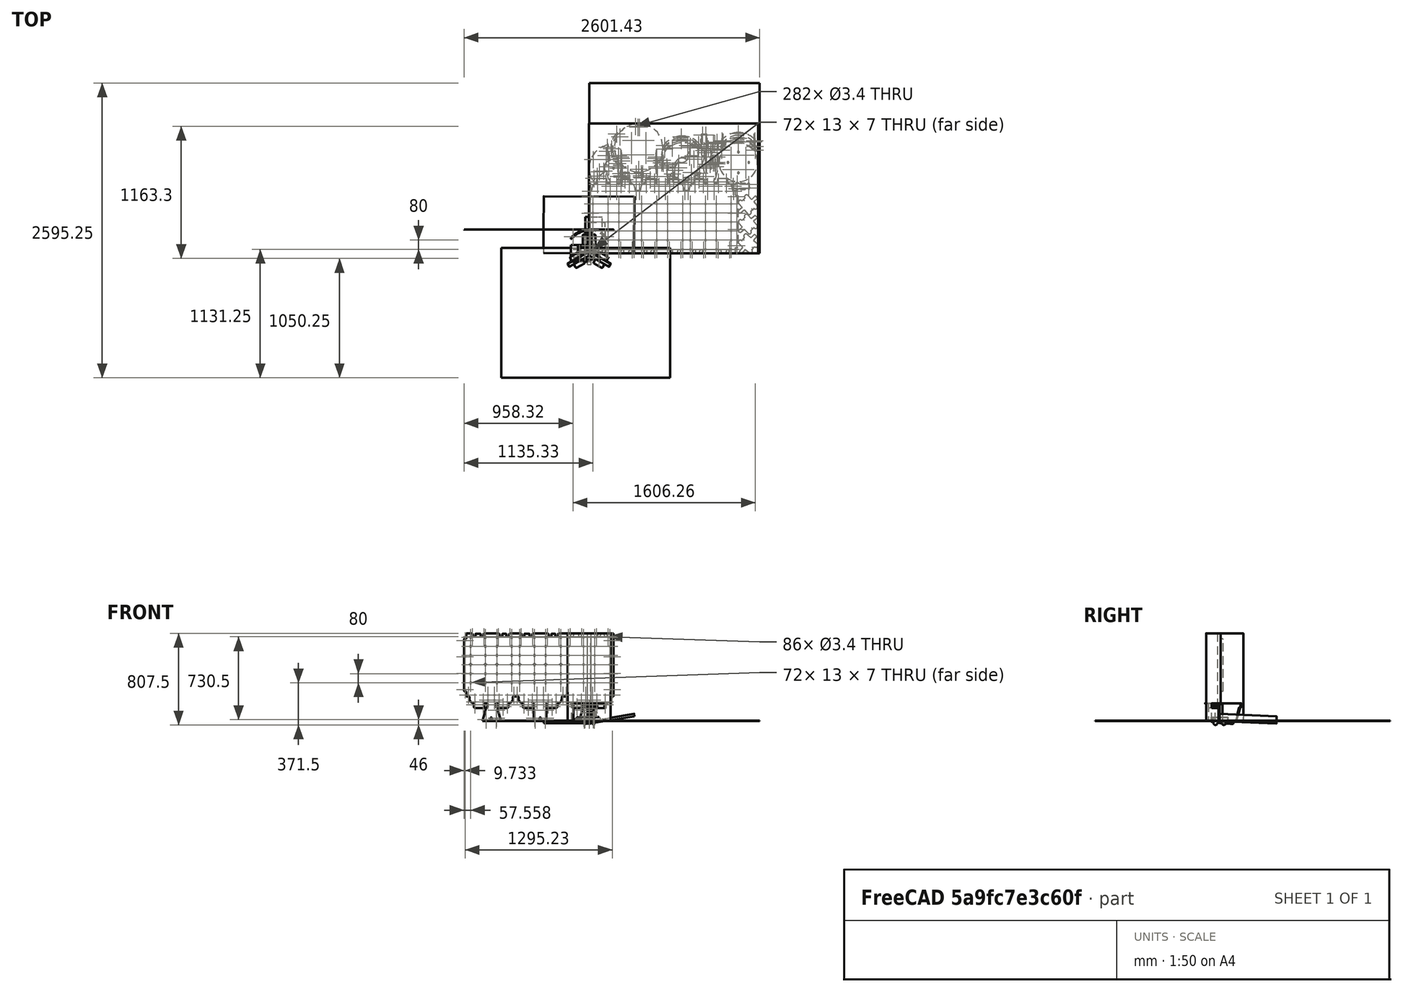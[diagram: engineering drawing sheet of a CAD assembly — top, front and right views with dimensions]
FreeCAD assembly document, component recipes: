
FREECAD ASSEMBLY — COMPONENT RECIPES ("composit_stand_small_3_vertDroppers")

This assembly document has 19 components, labeled P0..P18 below (a component is one placed body or linked part). 18 of them carry a construction recipe — the FreeCAD feature program that regenerates the part from scratch, quoted from this document or its linked companion documents; the rest are supplied as boundary geometry only. No exploded tour is included for this assembly.
NOTE — this tour is split across 2 documents so each fits a 32k-token context. This is document 1: the component sections continue in the remaining 1 document, each repeating the header above.
COMPONENT P0 — recipe-attached ("gutter001_material_0.50ansi", modeled in this document).
Construction recipe (the document's own serialized feature program — sketch geometry with constraints, then the solid features built on it; lengths are millimeters unless a unit is written):

FEATURE [Sketcher::SketchObject] Sketch  label="gutter_side_sketch"
  FullyConstrained = true
  MapMode = 5
  Support = -> [XY_Plane]
  expr: .AttachmentOffset.Base.x = 0
  expr: .Constraints.little_distance = <<gutter>>.low_edge_length + (<<main>>.inner_width - <<main>>.thickness * 2) / 2 - 3mm
  expr: Constraints[12] = <<gutter>>.length
  expr: Constraints[27] = <<gutter>>.bend_angle + 90°
  sketch-geometry (15):
    g0: LineSegment StartX=0 StartY=150 StartZ=0 EndX=13.5 EndY=150 EndZ=0
    g1: LineSegment StartX=27 StartY=0 StartZ=0 EndX=0 EndY=0 EndZ=0
    g2: LineSegment StartX=15 StartY=148.5 StartZ=0 EndX=15 EndY=120 EndZ=0
    g3: LineSegment StartX=15 StartY=120 StartZ=0 EndX=31.2589 EndY=120 EndZ=0
    g4: GeomPoint X=27 Y=150 Z=0
    g5: ArcOfCircle CenterX=31.2589 CenterY=116.5 CenterZ=0 NormalX=0 NormalY=0 NormalZ=1 AngleXU=0 Radius=3.5 StartAngle=6.21662 EndAngle=7.85398
    g6: GeomPoint X=27 Y=0 Z=0
    g7: ArcOfCircle CenterX=13.5 CenterY=148.5 CenterZ=0 NormalX=0 NormalY=0 NormalZ=1 AngleXU=0 Radius=1.5 StartAngle=-3.6e-15 EndAngle=1.5708
    g8: GeomPoint X=15 Y=150 Z=0
    g9: LineSegment StartX=34.7511 StartY=116.267 StartZ=0 EndX=27.4178 EndY=6.26718 EndZ=0
    g10: LineSegment StartX=27.4178 StartY=6.26718 StartZ=0 EndX=27 EndY=0 EndZ=0
    g11: ArcOfCircle CenterX=23.9256 CenterY=6.5 CenterZ=0 NormalX=0 NormalY=0 NormalZ=1 AngleXU=0 Radius=3.5 StartAngle=4.71239 EndAngle=6.21662
    g12: LineSegment StartX=0 StartY=0 StartZ=0 EndX=0 EndY=3 EndZ=0
    g13: LineSegment StartX=0 StartY=3 StartZ=0 EndX=0 EndY=150 EndZ=0
    g14: LineSegment StartX=0 StartY=3 StartZ=0 EndX=23.9256 EndY=3 EndZ=0
  constraints (36):
    c: Coincident(g-1,g12)
    c: PointOnObject(g13,g-2)
    c: Coincident(g13,g0)
    c: Horizontal(g0)
    c: PointOnObject(g6,g-1)
    c: Coincident(g1,g12)
    c: Distance(g1,g6) = 27  'little_distance'
    c: Vertical(g2)
    c: Coincident(g3,g2)
    c: Horizontal(g3)
    c: DistanceY(g2,g8) = 30
    c: PointOnObject(g4,g0)
    c: Distance(g6,g4) = 150
    c: Distance(g0,g8) = 15
    c: Tangent(g3,g5) = 1.5708
    c: Diameter(g5) = 7
    c: PointOnObject(g8,g0)
    c: PointOnObject(g8,g2)
    c: Tangent(g0,g7) = 1.5708
    c: Tangent(g2,g7) = 1.5708
    c: Diameter(g7) = 3
    c: Tangent(g9,g5) = 1.5708
    c: Vertical(g4,g6)
    c: Coincident(g1,g6)
    c: Coincident(g10,g1)
    c: Coincident(g9,g10)
    c: Parallel(g9,g10)
    c: Angle(g10,g-1) = 1.63736
    c: Coincident(g12,g13)
    c: Vertical(g12)
    c: Coincident(g14,g12)
    c: Horizontal(g14)
    c: Tangent(g11,g9) = 1.5708
    c: Tangent(g14,g11) = -1.5708
    c: Equal(g11,g5)
    c: DistanceY(g12,g12) = 3
FEATURE [PartDesign::Pad] Pad  label="gutter_side_pad"
  Direction = (0,0,1)
  Length = 0.3
  Length2 = 10
  Profile = -> Sketch
  ReferenceAxis = -> Sketch [N_Axis]
  Type = 0
FEATURE [Sketcher::SketchObject] Sketch010
  FullyConstrained = true
  MapMode = 5
  Support = -> [XY_Plane]
  expr: Constraints[2] = -(<<main>>.inner_width / 2 - <<main>>.thickness - <<main>>.bend_r)
  expr: Constraints[3] = <<gutter>>.length
  sketch-geometry (1):
    g0: LineSegment StartX=-9.99 StartY=0 StartZ=0 EndX=-9.99 EndY=150 EndZ=0
  constraints (4):
    c: PointOnObject(g0,g-1)
    c: Vertical(g0)
    c: DistanceX(g0) = -9.99
    c: DistanceY(g0) = 150
FEATURE [PartDesign::Mirrored] Mirrored005
  BaseFeature = -> Pad
  MirrorPlane = -> YZ_Plane
  Originals = -> [Pad]
  Refine = true
FEATURE [PartDesign::CoordinateSystem] Local_CS001
  AttacherType = Attacher::AttachEngine3D
  AttachmentOffset = pos=(-30,0,0) rot=(0,0,1;0.066568rad)
  MapMode = 5
  Placement = pos=(-30,0,0) rot=(0,0,1;0.066568rad)
  Support = -> [XY_Plane]
  expr: .AttachmentOffset.Base.x = -(<<gutter>>.low_edge_length + (<<main>>.inner_width - <<main>>.thickness * 2) / 2)
  expr: .AttachmentOffset.Rotation.Angle = <<gutter>>.bend_angle
  expr: .AttachmentOffset.Rotation.Yaw = <<gutter>>.bend_angle
FEATURE [PartDesign::CoordinateSystem] Local_CS002
  AttacherType = Attacher::AttachEngine3D
  AttachmentOffset = pos=(30,0,0) rot=(0,0,1;-0.066568rad)
  MapMode = 5
  Placement = pos=(30,0,0) rot=(0,0,1;6.21662rad)
  Support = -> [XY_Plane]
  expr: .AttachmentOffset.Base.x = <<gutter>>.low_edge_length + (<<main>>.inner_width - <<main>>.thickness * 2) / 2
  expr: .AttachmentOffset.Rotation.Angle = -<<gutter>>.bend_angle
FEATURE [PartDesign::CoordinateSystem] Local_CS003
  AttacherType = Attacher::AttachEngine3D
  AttachmentOffset = pos=(0,60,0) rot=(0,0,1;1.5708rad)
  MapMode = 5
  Placement = pos=(33.9911,59.8671,0) rot=(0,0,1;1.50423rad)
  Support = -> [Local_CS002]
  expr: .AttachmentOffset.Base.y = <<gutter>>.plane_middle
FEATURE [PartDesign::CoordinateSystem] Local_CS004
  AttacherType = Attacher::AttachEngine3D
  AttachmentOffset = pos=(2,60,0) rot=(0,0,1;-1.5708rad)
  MapMode = 5
  Placement = pos=(-31.9956,60.0001,0) rot=(0,0,1;4.77896rad)
  Support = -> [Local_CS001]
  expr: .AttachmentOffset.Base.y = <<gutter>>.plane_middle
FEATURE [PartDesign::Plane] DatumPlane003
  Length = 91.4351
  MapMode = 4
  Placement = pos=(33.9911,59.8671,0) rot=(0.023538,0.706911,0.706911;3.09453rad)
  ResizeMode = 0
  Support = -> [Local_CS003]
  Width = 62.5599
FEATURE [PartDesign::Plane] DatumPlane004
  Length = 91.4351
  MapMode = 4
  Placement = pos=(-31.9956,60.0001,0) rot=(0.998893,0.03326,0.03326;1.5719rad)
  ResizeMode = 0
  Support = -> [Local_CS004]
  Width = 62.5599
FEATURE [PartDesign::Plane] DatumPlane005
  AttachmentOffset = pos=(0,-1,0) rot=(0,0,1;0rad)
  Length = 202.865
  MapMode = 5
  Placement = pos=(34.9889,59.8006,0) rot=(0,0,1;1.50423rad)
  ResizeMode = 0
  Support = -> [Local_CS003]
  Width = 102.646
FEATURE [PartDesign::Plane] DatumPlane006
  Length = 202.865
  MapMode = 5
  Placement = pos=(-31.9956,60.0001,0) rot=(0,0,-1;1.50423rad)
  ResizeMode = 0
  Support = -> [Local_CS004]
  Width = 102.646
FEATURE [Sketcher::SketchObject] Sketch037
  AttachmentOffset = pos=(30,2,0) rot=(0,0,1;0rad)
  FullyConstrained = true
  MapMode = 5
  Placement = pos=(33.9911,89.9337,0) rot=(0,0,1;1.50423rad)
  Support = -> [Local_CS003]
  expr: .AttachmentOffset.Base.x = <<dropper>>.distance_between_droppers1 / 2
  expr: Constraints[10] = <<dropper>>.d
  sketch-geometry (8):
    g0: LineSegment StartX=0 StartY=11.625 StartZ=0 EndX=1 EndY=11.625 EndZ=0
    g1: ArcOfCircle CenterX=1 CenterY=0 CenterZ=0 NormalX=0 NormalY=0 NormalZ=1 AngleXU=0 Radius=11.625 StartAngle=0.450911 EndAngle=1.5708
    g2: ArcOfCircle CenterX=17.127 CenterY=0 CenterZ=0 NormalX=0 NormalY=0 NormalZ=1 AngleXU=0 Radius=3 StartAngle=0.25268 EndAngle=1.29556
    g3: LineSegment StartX=12.0914 StartY=4.53943 StartZ=0 EndX=17.9423 EndY=2.88708 EndZ=0
    g4: LineSegment StartX=0 StartY=11.625 StartZ=0 EndX=0 EndY=0 EndZ=0
    g5: LineSegment StartX=0 StartY=0 StartZ=0 EndX=21 EndY=0 EndZ=0
    g6: ArcOfCircle CenterX=21 CenterY=1 CenterZ=0 NormalX=0 NormalY=0 NormalZ=1 AngleXU=0 Radius=1 StartAngle=3.39427 EndAngle=4.71239
    g7: ArcOfCircle CenterX=12.3631 CenterY=5.5018 CenterZ=0 NormalX=0 NormalY=0 NormalZ=1 AngleXU=0 Radius=1 StartAngle=3.5925 EndAngle=4.43715
  constraints (22):
    c: PointOnObject(g0,g-2)
    c: Horizontal(g0)
    c: PointOnObject(g2,g-1)
    c: Tangent(g3,g2) = 1.5708
    c: Tangent(g1,g0) = 1.5708
    c: Coincident(g4,g0)
    c: Coincident(g4,g-1)
    c: Coincident(g5,g4)
    c: Diameter(g2) = 6
    c: Angle(g3,g-1) = 0.275238
    c: Diameter(g1) = 23.25
    c: PointOnObject(g1,g-1)
    c: Distance(g0) = 1
    c: Horizontal(g5)
    c: Tangent(g6,g5) = -1.5708
    c: Tangent(g6,g2) = 1.5708
    c: Diameter(g6) = 2
    c: Distance(g5) = 21
    c: Tangent(g3,g7) = -1.5708
    c: Tangent(g1,g7) = 1.5708
    c: Diameter(g7) = 2
    c: DistanceY(g2) = 2.88708  'arc_height'
FEATURE [PartDesign::Pocket] Pocket008
  BaseFeature = -> Mirrored005
  Direction = (0,0,-1)
  Length = 5
  Length2 = 5
  Midplane = true
  Profile = -> Sketch037
  ReferenceAxis = -> Sketch037 [N_Axis]
  Type = 1
FEATURE [PartDesign::Mirrored] Mirrored006
  MirrorPlane = -> Sketch037 [V_Axis]
FEATURE [PartDesign::Mirrored] Mirrored007
  MirrorPlane = -> DatumPlane003
FEATURE [PartDesign::MultiTransform] MultiTransform002
  BaseFeature = -> Pocket008
  Originals = -> [Pocket008]
  Transformations = -> [Mirrored006,Mirrored007]
FEATURE [PartDesign::SubShapeBinder] Binder
  AttacherType = Attacher::AttachEngine3D
  AttachmentOffset = pos=(35,0,0) rot=(0,0,1;0rad)
  BindCopyOnChange = 0
  BindMode = 0
  ClaimChildren = true
  Context = -> Body [Binder.]
  Fuse = false
  MakeFace = true
  MapMode = 5
  OffsetFill = false
  OffsetIntersection = false
  OffsetJoinType = 0
  OffsetOpenResult = false
  PartialLoad = false
  Placement = pos=(-28.1674,25.0777,0) rot=(0,0,-1;1.50423rad)
  Relative = false
  _Version = 2
  expr: .AttachmentOffset.Base.x = <<dropper>>.distance_between_droppers2 / 2
FEATURE [PartDesign::Pocket] Pocket009
  BaseFeature = -> MultiTransform002
  Direction = (0,0,-1)
  Length = 5
  Length2 = 5
  Midplane = true
  Profile = -> Binder
  Type = 1
FEATURE [PartDesign::Plane] DatumPlane007
  Length = 91.4351
  MapMode = 4
  Placement = pos=(-28.1674,25.0777,0) rot=(0.998893,0.03326,0.03326;1.5719rad)
  ResizeMode = 0
  Support = -> [Binder]
  Width = 62.5599
FEATURE [PartDesign::Mirrored] Mirrored008
  MirrorPlane = -> DatumPlane007
FEATURE [PartDesign::Mirrored] Mirrored009
  MirrorPlane = -> DatumPlane004
FEATURE [PartDesign::MultiTransform] MultiTransform003
  BaseFeature = -> Pocket009
  Originals = -> [Pocket009]
  Transformations = -> [Mirrored008,Mirrored009]
FEATURE [Sketcher::SketchObject] Sketch038
  FullyConstrained = true
  MapMode = 5
  Support = -> [XY_Plane]
  expr: Constraints[2] = <<main>>.inner_width / 2 - <<main>>.thickness - <<main>>.bend_r
  expr: Constraints[3] = <<gutter>>.length
  sketch-geometry (1):
    g0: LineSegment StartX=9.99 StartY=0 StartZ=0 EndX=9.99 EndY=150 EndZ=0
  constraints (4):
    c: PointOnObject(g0,g-1)
    c: Vertical(g0)
    c: DistanceX(g0) = 9.99
    c: DistanceY(g0) = 150
FEATURE [Sketcher::SketchObject] Sketch039
  AttachmentOffset = pos=(51,14,0) rot=(0,0,1;0rad)
  FullyConstrained = true
  MapMode = 5
  Placement = pos=(24.4124,111.619,0) rot=(0,0,1;1.50423rad)
  Support = -> [DatumPlane005]
  expr: .AttachmentOffset.Base.x = <<main>>.gutter_fix_holes_distance
  expr: Constraints[1] = <<main>>.rivet_d
  sketch-geometry (1):
    g0: Circle CenterX=0 CenterY=0 CenterZ=0 NormalX=0 NormalY=0 NormalZ=1 AngleXU=0 Radius=1.7
  constraints (2):
    c: Coincident(g0,g-1)
    c: Diameter(g0) = 3.4
FEATURE [PartDesign::Pocket] Pocket010
  BaseFeature = -> MultiTransform003
  Direction = (0,0,-1)
  Length = 5
  Length2 = 5
  Midplane = true
  Profile = -> Sketch039
  ReferenceAxis = -> Sketch039 [N_Axis]
  Type = 1
FEATURE [PartDesign::Mirrored] Mirrored010
  MirrorPlane = -> DatumPlane003
FEATURE [PartDesign::Mirrored] Mirrored011
  MirrorPlane = -> YZ_Plane
FEATURE [PartDesign::MultiTransform] MultiTransform004
  BaseFeature = -> Pocket010
  Originals = -> [Pocket010]
  Transformations = -> [Mirrored010,Mirrored011]
FEATURE [PartDesign::FeaturePython] Fold  # WARN: FeaturePython — macro-defined, semantics opaque (R4)
  BaseFeature = -> MultiTransform004
  BendLine = -> Sketch038
  Position = 0
  angle = 90
  baseObject = -> MultiTransform004 [Face4]
  invert = false
  invertbend = true
  kfactor = 0.01
  radius = 0.01
  unfold = false
  expr: radius = <<main>>.bend_r
FEATURE [PartDesign::FeaturePython] Fold002  # WARN: FeaturePython — macro-defined, semantics opaque (R4)
  BaseFeature = -> Fold
  BendLine = -> Sketch010
  Position = 0
  angle = 90
  baseObject = -> Fold [Face2]
  invert = false
  invertbend = false
  kfactor = 0.01
  radius = 0.01
  unfold = false
  expr: radius = <<main>>.bend_r
FEATURE [PartDesign::CoordinateSystem] Local_CS024
  AttacherType = Attacher::AttachEngine3D
  AttachmentOffset = pos=(0,60,-10.3215) rot=(-1,0,0;0.066568rad)
  MapMode = 5
  Placement = pos=(0,60,-10.3215) rot=(-1,0,0;0.066568rad)
  Support = -> [XY_Plane]
  expr: .AttachmentOffset.Base.y = <<gutter>>.plane_middle
  expr: .AttachmentOffset.Base.z = (-6.929mm - 13.714mm) / 2
  expr: .AttachmentOffset.Rotation.Roll = -<<gutter>>.bend_angle
FEATURE [Sketcher::SketchObject] Sketch115
  FullyConstrained = true
  MapMode = 5
  Support = -> [XY_Plane]
  expr: Constraints[1] = <<main>>.rivet_d
  sketch-geometry (1):
    g0: Circle CenterX=0 CenterY=145 CenterZ=0 NormalX=0 NormalY=0 NormalZ=1 AngleXU=0 Radius=1.7
  constraints (3):
    c: PointOnObject(g0,g-2)
    c: Diameter(g0) = 3.4
    c: DistanceY(g0) = 145
FEATURE [PartDesign::Pocket] Pocket070
  BaseFeature = -> Fold002
  Direction = (0,0,-1)
  Length = 5
  Length2 = 5
  Midplane = true
  Profile = -> Sketch115
  ReferenceAxis = -> Sketch115 [N_Axis]
  Type = 1
FEATURE [PartDesign::Body] Body  label="gutter001_material_0.50ansi"
  Group = -> [Sketch,Pad,Mirrored005,Local_CS001,Local_CS002,Local_CS003,Local_CS004,DatumPlane003,DatumPlane004,DatumPlane005,DatumPlane006,Sketch037,Pocket008,MultiTransform002,Mirrored006,Mirrored007,Binder,Pocket009,MultiTransform003,Mirrored008,DatumPlane007,Mirrored009,Sketch010,Sketch038,Sketch039,Pocket010,MultiTransform004,Mirrored010,Mirrored011,Fold,Fold002,Local_CS024,Sketch115,Pocket070]
  Origin = -> Origin
  Tip = -> Pocket070
COMPONENT P1 — recipe-attached ("Body001_material_0.30ansi", modeled in this document).
Construction recipe (the document's own serialized feature program — sketch geometry with constraints, then the solid features built on it; lengths are millimeters unless a unit is written):

FEATURE [Sketcher::SketchObject] Sketch003  label="main_sketch"
  FullyConstrained = true
  MapMode = 5
  Support = -> [XY_Plane001]
  expr: Constraints[30] = <<main>>.end_face_width
  expr: Constraints[31] = <<main>>.work_plane_width
  expr: Constraints[44] = <<main>>.al_thickness
  sketch-geometry (17):
    g0: LineSegment StartX=-16 StartY=9.2376 StartZ=0 EndX=-16 EndY=209.238 EndZ=0
    g1: LineSegment StartX=-16 StartY=209.238 StartZ=0 EndX=16 EndY=209.238 EndZ=0
    g2: LineSegment StartX=16 StartY=209.238 StartZ=0 EndX=16 EndY=9.2376 EndZ=0
    g3: LineSegment StartX=16 StartY=9.2376 StartZ=0 EndX=189.205 EndY=-90.7624 EndZ=0
    g4: LineSegment StartX=189.205 StartY=-90.7624 StartZ=0 EndX=173.205 EndY=-118.475 EndZ=0
    g5: LineSegment StartX=173.205 StartY=-118.475 StartZ=0 EndX=0 EndY=-18.4752 EndZ=0
    g6: LineSegment StartX=0 StartY=-18.4752 StartZ=0 EndX=-173.205 EndY=-118.475 EndZ=0
    g7: LineSegment StartX=-173.205 StartY=-118.475 StartZ=0 EndX=-189.205 EndY=-90.7624 EndZ=0
    g8: LineSegment StartX=-189.205 StartY=-90.7624 StartZ=0 EndX=-16 EndY=9.2376 EndZ=0
    g9: LineSegment StartX=-16 StartY=9.2376 StartZ=0 EndX=0 EndY=0 EndZ=0
    g10: LineSegment StartX=0 StartY=0 StartZ=0 EndX=16 EndY=9.2376 EndZ=0
    g11: LineSegment StartX=0 StartY=0 StartZ=0 EndX=0 EndY=-18.4752 EndZ=0
    g12: LineSegment StartX=189.205 StartY=-90.7624 StartZ=0 EndX=13 EndY=10.9697 EndZ=0
    g13: LineSegment StartX=16 StartY=209.238 StartZ=0 EndX=16 EndY=9.42236 EndZ=0
    g14: LineSegment StartX=16 StartY=9.42236 StartZ=0 EndX=15.7 EndY=9.42236 EndZ=0
    g15: LineSegment StartX=13 StartY=10.9697 StartZ=0 EndX=13 EndY=30.9697 EndZ=0
    g16: LineSegment StartX=13 StartY=10.9697 StartZ=0 EndX=6.66667 EndY=0 EndZ=0
  constraints (56):
    c: Vertical(g0)
    c: Coincident(g0,g1)
    c: Horizontal(g1)
    c: Coincident(g1,g2)
    c: Vertical(g2)
    c: Coincident(g2,g3)
    c: Coincident(g3,g4)
    c: Coincident(g4,g5)
    c: PointOnObject(g5,g-2)
    c: Coincident(g5,g6)
    c: Coincident(g6,g7)
    c: Coincident(g8,g7)
    c: Equal(g2,g6)
    c: Equal(g6,g5)
    c: Equal(g5,g3)
    c: Equal(g4,g7)
    c: Equal(g7,g1)
    c: Perpendicular(g4,g5)
    c: Perpendicular(g4,g3)
    c: Perpendicular(g7,g6)
    c: Perpendicular(g8,g7)
    c: Angle(g6,g5) = 2.0944
    c: Angle(g3,g2) = 2.0944
    c: Coincident(g9,g0)
    c: Coincident(g9,g-1)
    c: Coincident(g10,g9)
    c: Coincident(g10,g2)
    c: Coincident(g11,g9)
    c: Coincident(g11,g5)
    c: Equal(g10,g11)
    c: DistanceX(g1,g1) = 32
    c: DistanceY(g2,g2) = 200
    c: DistanceY(g9,g2) = 9.2376  'petal_offset'
    c: DistanceY(g0) = 9.2376  'petal_conn_y'
    c: Coincident(g8,g0)
    c: DistanceX(g2) = 16  'petal_conn_x'
    c: Distance(g9,g1) = 209.848  'max_r'
    c: Distance(g10) = 18.4752  'planes_intersec_r'
    c: DistanceY(g9,g1) = 209.238  'total_petal_length'
    c: Coincident(g12,g4)
    c: Coincident(g13,g1)
    c: PointOnObject(g13,g2)
    c: Coincident(g14,g13)
    c: Horizontal(g14)
    c: DistanceX(g14,g14) = 0.3
    c: Distance(g14,g12) = 0.01
    c: PointOnObject(g2,g12)
    c: Distance(g12,g13) = 3
    c: Coincident(g15,g12)
    c: Vertical(g15)
    c: DistanceY(g15,g15) = 20
    c: DistanceY(g15) = 30.9697  'overlap_end_y'
    c: Coincident(g16,g12)
    c: Perpendicular(g16,g12)
    c: Distance(g9,g16) = 5.7735  'overlap_bend_offset'
    c: PointOnObject(g16,g-1)
FEATURE [PartDesign::FeaturePython] BaseBend001  # WARN: FeaturePython — macro-defined, semantics opaque (R4)
  BendSide = 0
  BendSketch = -> Sketch003
  MidPlane = false
  Reverse = false
  length = 774
  radius = 0.01
  thickness = 0.3
  expr: length = <<main>>.total_length
  expr: radius = <<main>>.bend_r
FEATURE [PartDesign::CoordinateSystem] Local_CS
  AttacherType = Attacher::AttachEngine3D
  AttachmentOffset = pos=(0,9.2376,0) rot=(0,0,1;0rad)
  MapMode = 5
  Placement = pos=(0,9.2376,0) rot=(0,0,1;0rad)
  Support = -> [XY_Plane001]
  expr: .AttachmentOffset.Base.y = Sketch003.Constraints.petal_offset
FEATURE [PartDesign::CoordinateSystem] Local_CS011
  AttacherType = Attacher::AttachEngine3D
  AttachmentOffset = pos=(0,100,0) rot=(0,0,1;0rad)
  MapMode = 5
  Placement = pos=(0,109.238,0) rot=(0,0,1;0rad)
  Support = -> [Local_CS]
  expr: .AttachmentOffset.Base.y = <<main>>.work_plane_width / 2
FEATURE [PartDesign::Plane] DatumPlane011
  AttachmentOffset = pos=(0,0,0) rot=(0,0,1;0.523599rad)
  Length = 594.137
  MapMode = 5
  Placement = pos=(0,0,0) rot=(0,0,1;0.523599rad)
  ResizeMode = 0
  Support = -> [XY_Plane001]
  Width = 579.207
FEATURE [PartDesign::CoordinateSystem] Local_CS035
  AttacherType = Attacher::AttachEngine3D
  AttachmentOffset = pos=(0,0,774) rot=(0,0,1;0rad)
  MapMode = 5
  Placement = pos=(0,109.238,774) rot=(0,0,1;0rad)
  Support = -> [Local_CS011]
  expr: .AttachmentOffset.Base.z = <<main>>.total_length
FEATURE [PartDesign::CoordinateSystem] Local_CS036  label="droppers_center"
  AttacherType = Attacher::AttachEngine3D
  AttachmentOffset = pos=(0,0,-19) rot=(0,0,1;0rad)
  MapMode = 5
  Placement = pos=(0,109.238,755) rot=(0,0,1;0rad)
  Support = -> [Local_CS035]
FEATURE [PartDesign::CoordinateSystem] Local_CS037  label="gutter_fixture_center"
  AttacherType = Attacher::AttachEngine3D
  AttachmentOffset = pos=(0,0,-12) rot=(0,0,1;0rad)
  MapMode = 5
  Placement = pos=(0,109.238,743) rot=(0,0,1;0rad)
  Support = -> [Local_CS036]
FEATURE [PartDesign::CoordinateSystem] Local_CS038  label="modules_top_center"
  AttacherType = Attacher::AttachEngine3D
  AttachmentOffset = pos=(0,0,-5) rot=(0,0,1;0rad)
  MapMode = 5
  Placement = pos=(0,109.238,738) rot=(0,0,1;0rad)
  Support = -> [Local_CS037]
FEATURE [Sketcher::SketchObject] Sketch112
  FullyConstrained = true
  MapMode = 5
  Placement = pos=(0,0,0) rot=(0.57735,0.57735,0.57735;2.0944rad)
  Support = -> [YZ_Plane001]
  expr: Constraints[10] = <<module>>.module_hole_x
  expr: Constraints[11] = <<module>>.module_hole_y
  sketch-geometry (5):
    g0: LineSegment StartX=-6.5 StartY=-3.5 StartZ=0 EndX=-6.5 EndY=3.5 EndZ=0
    g1: LineSegment StartX=-6.5 StartY=3.5 StartZ=0 EndX=6.5 EndY=3.5 EndZ=0
    g2: LineSegment StartX=6.5 StartY=3.5 StartZ=0 EndX=6.5 EndY=-3.5 EndZ=0
    g3: LineSegment StartX=6.5 StartY=-3.5 StartZ=0 EndX=-6.5 EndY=-3.5 EndZ=0
    g4: GeomPoint X=0 Y=0 Z=0
  constraints (12):
    c: Coincident(g0,g1)
    c: Coincident(g1,g2)
    c: Coincident(g2,g3)
    c: Coincident(g3,g0)
    c: Horizontal(g1)
    c: Horizontal(g3)
    c: Vertical(g0)
    c: Vertical(g2)
    c: Symmetric(g1,g0,g4)
    c: Coincident(g4,g-1)
    c: DistanceX(g1,g1) = 13
    c: DistanceY(g2,g2) = 7
FEATURE [Sketcher::SketchObject] Sketch113
  FullyConstrained = true
  MapMode = 5
  Placement = pos=(0,0,0) rot=(0.57735,0.57735,0.57735;2.0944rad)
  Support = -> [YZ_Plane001]
  expr: Constraints[18] = <<dropper>>.d + 2mm
  expr: Constraints[19] = <<dropper>>.center_height_offset
  sketch-geometry (8):
    g0: ArcOfCircle CenterX=0 CenterY=0 CenterZ=0 NormalX=0 NormalY=0 NormalZ=1 AngleXU=0 Radius=12.625 StartAngle=3.14159 EndAngle=6.28319
    g1: LineSegment StartX=12.625 StartY=-3.1e-15 StartZ=0 EndX=12.625 EndY=12.5 EndZ=0
    g2: LineSegment StartX=-12.625 StartY=1.5e-15 StartZ=0 EndX=-12.625 EndY=12.5 EndZ=0
    g3: ArcOfCircle CenterX=15.125 CenterY=12.5 CenterZ=0 NormalX=0 NormalY=0 NormalZ=1 AngleXU=0 Radius=2.5 StartAngle=1.5708 EndAngle=3.14159
    g4: ArcOfCircle CenterX=-15.125 CenterY=12.5 CenterZ=0 NormalX=0 NormalY=0 NormalZ=1 AngleXU=0 Radius=2.5 StartAngle=0 EndAngle=1.5708
    g5: LineSegment StartX=-15.125 StartY=15 StartZ=0 EndX=-15.125 EndY=19 EndZ=0
    g6: LineSegment StartX=-15.125 StartY=19 StartZ=0 EndX=15.125 EndY=19 EndZ=0
    g7: LineSegment StartX=15.125 StartY=19 StartZ=0 EndX=15.125 EndY=15 EndZ=0
  constraints (24):
    c: Coincident(g0,g-1)
    c: PointOnObject(g0,g-1)
    c: PointOnObject(g0,g-1)
    c: Coincident(g1,g0)
    c: Vertical(g1)
    c: Coincident(g2,g0)
    c: Vertical(g2)
    c: Coincident(g5,g4)
    c: Vertical(g5)
    c: Coincident(g6,g5)
    c: Horizontal(g6)
    c: Coincident(g7,g6)
    c: Coincident(g7,g3)
    c: Vertical(g7)
    c: Perpendicular(g3,g7)
    c: Tangent(g3,g1) = 1.5708
    c: Tangent(g4,g2) = -1.5708
    c: Perpendicular(g4,g5)
    c: Diameter(g0) = 25.25
    c: Distance(g0,g6) = 19
    c: Equal(g4,g3)
    c: Diameter(g4) = 5
    c: DistanceY(g7,g7) = 4
    c: Equal(g5,g7)
FEATURE [Sketcher::SketchObject] Sketch128
  FullyConstrained = true
  MapMode = 5
  Placement = pos=(0,0,0) rot=(0.57735,0.57735,0.57735;2.0944rad)
  Support = -> [YZ_Plane001]
  expr: Constraints[5] = <<main>>.basin_height
  sketch-geometry (5):
    g0: LineSegment StartX=73 StartY=116.5 StartZ=0 EndX=166 EndY=116.5 EndZ=0
    g1: LineSegment StartX=166 StartY=116.5 StartZ=0 EndX=166 EndY=157 EndZ=0
    g2: LineSegment StartX=166 StartY=157 StartZ=0 EndX=73 EndY=157 EndZ=0
    g3: LineSegment StartX=73 StartY=157 StartZ=0 EndX=73 EndY=116.5 EndZ=0
    g4: GeomPoint X=119.5 Y=157 Z=0
  constraints (15):
    c: Coincident(g0,g1)
    c: Coincident(g1,g2)
    c: Coincident(g2,g3)
    c: Coincident(g3,g0)
    c: DistanceX(g0) = 73  'offset_x'
    c: DistanceY(g2) = 157
    c: Distance(g3) = 40.5  'height'
    c: Distance(g0) = 93  'length'
    c: Parallel(g1,g3)
    c: Parallel(g0,g2)
    c: Perpendicular(g0,g3)
    c: Angle(g-1,g0) = 0
    c: Symmetric(g2,g1,g4)
    c: DistanceX(g4) = 119.5  'top_center_x'
    c: DistanceY(g4) = 157  'top_center_y'
FEATURE [PartDesign::Pocket] Pocket081
  BaseFeature = -> BaseBend001
  Direction = (-1,2e-16,-3e-16)
  Length = 5
  Length2 = 5
  Midplane = true
  Profile = -> Sketch128
  ReferenceAxis = -> Sketch128 [N_Axis]
  Type = 1
FEATURE [PartDesign::PolarPattern] PolarPattern016
  Angle = 360
  Axis = -> Z_Axis001
  BaseFeature = -> Pocket081
  Occurrences = 3
  Originals = -> [Pocket081]
FEATURE [PartDesign::FeaturePython] Bend  # WARN: FeaturePython — macro-defined, semantics opaque (R4)
  AutoMiter = true
  BaseFeature = -> PolarPattern016
  BendType = 0
  LengthList = [40]
  LengthSpec = 2
  ReliefFactor = 0.7
  UseReliefFactor = false
  angle = 90
  baseObject = -> PolarPattern016 [Edge67,Edge25,Edge211,Edge168,Edge96,Edge140]
  bendAList = [90]
  extend1 = 0
  extend2 = 0
  gap1 = 0.1
  gap2 = 0.1
  invert = false
  kfactor = 0.5
  length = 40
  maxExtendDist = 5
  minGap = 0.1
  minReliefGap = 1
  miterangle1 = 0
  miterangle2 = 0
  offset = 0
  radius = 0.1
  reliefType = 0
  reliefd = 1
  reliefw = 0.8
  sketchflip = false
  sketchinvert = false
  unfold = false
  expr: angle = 90deg - <<main>>.cover_bend_mid
FEATURE [PartDesign::Pocket] Pocket007
  BaseFeature = -> Bend
  Direction = (-1,2e-16,-3e-16)
  Length = 13.01
  Length2 = 5
  Profile = -> Sketch012
  ReferenceAxis = -> Sketch012 [N_Axis]
  Reversed = true
  Type = 0
  expr: Length = <<main>>.end_face_width / 2 - <<main>>.thickness + <<main>>.bend_r
FEATURE [Sketcher::SketchObject] Sketch129
  AttachmentOffset = pos=(0,0,0) rot=(0,1,0;3.66519rad)
  FullyConstrained = true
  MapMode = 5
  Placement = pos=(0,0,0) rot=(-0.186157,0.694747,0.694747;3.50969rad)
  Support = -> [XZ_Plane001]
  expr: .Constraints.height = Sketch128.Constraints.height
  expr: .Constraints.length = Sketch128.Constraints.length
  expr: Constraints[20] = <<main>>.cover_plane_bend
  expr: Constraints[24] = Sketch128.Constraints.top_center_x
  expr: Constraints[25] = Sketch128.Constraints.top_center_y
  expr: Constraints[8] = <<main>>.basin_height
  sketch-geometry (10):
    g0: LineSegment StartX=0 StartY=0 StartZ=0 EndX=169.18 EndY=0 EndZ=0
    g1: LineSegment StartX=169.18 StartY=0 StartZ=0 EndX=169.18 EndY=157 EndZ=0
    g2: LineSegment StartX=0 StartY=157 StartZ=0 EndX=0 EndY=0 EndZ=0
    g3: LineSegment StartX=73 StartY=116.5 StartZ=0 EndX=166 EndY=116.5 EndZ=0
    g4: LineSegment StartX=166 StartY=116.5 StartZ=0 EndX=166 EndY=157 EndZ=0
    g5: LineSegment StartX=166 StartY=157 StartZ=0 EndX=73 EndY=157 EndZ=0
    g6: LineSegment StartX=73 StartY=157 StartZ=0 EndX=73 EndY=116.5 EndZ=0
    g7: LineSegment StartX=169.18 StartY=157 StartZ=0 EndX=166 EndY=157 EndZ=0
    g8: LineSegment StartX=73 StartY=157 StartZ=0 EndX=0 EndY=157 EndZ=0
    g9: GeomPoint X=119.5 Y=157 Z=0
  constraints (26):
    c: Coincident(g0,g1)
    c: Coincident(g1,g7)
    c: Coincident(g8,g2)
    c: Coincident(g2,g0)
    c: Horizontal(g0)
    c: Vertical(g1)
    c: Vertical(g2)
    c: Coincident(g0,g-1)
    c: DistanceY(g8) = 157
    c: Coincident(g3,g4)
    c: Coincident(g4,g5)
    c: Coincident(g5,g6)
    c: Coincident(g6,g3)
    c: Horizontal(g7)
    c: Coincident(g8,g5)
    c: Coincident(g7,g4)
    c: Perpendicular(g4,g3)
    c: Perpendicular(g5,g4)
    c: Perpendicular(g5,g6)
    c: Distance(g3,g1) = 3.18
    c: Angle(g-1,g5) = 0
    c: Distance(g6) = 40.5  'height'
    c: Distance(g3) = 93  'length'
    c: Symmetric(g6,g4,g9)
    c: DistanceX(g9) = 119.5
    c: DistanceY(g9) = 157
FEATURE [PartDesign::CoordinateSystem] Local_CS041
  AttacherType = Attacher::AttachEngine3D
  AttachmentOffset = pos=(119.5,157,16) rot=(0,-0.707107,-0.707107;3.14159rad)
  MapMode = 5
  Placement = pos=(16,119.5,157) rot=(0,0,-1;1.5708rad)
  Support = -> [YZ_Plane001]
  expr: .AttachmentOffset.Base.x = Sketch128.Constraints.top_center_x
  expr: .AttachmentOffset.Base.y = Sketch128.Constraints.top_center_y
  expr: .AttachmentOffset.Base.z = <<main>>.end_face_width / 2
FEATURE [PartDesign::CoordinateSystem] Local_CS039
  AttacherType = Attacher::AttachEngine3D
  AttachmentOffset = pos=(0,-3,-3) rot=(0,1,0.71;0rad)
  MapMode = 5
  Placement = pos=(13,119.5,154) rot=(0,0,-1;1.5708rad)
  Support = -> [Local_CS041]
  expr: .AttachmentOffset.Base.y = -<<main>>.thickness
  expr: .AttachmentOffset.Base.z = -<<main>>.thickness
FEATURE [Sketcher::SketchObject] Sketch130
  AttachmentOffset = pos=(0,40.5,0) rot=(0,0,1;0rad)
  FullyConstrained = true
  MapMode = 5
  Placement = pos=(56.5,119.5,157) rot=(0,0,-1;1.5708rad)
  Support = -> [Local_CS041]
  expr: .AttachmentOffset.Base.y = Bend.length + 0.5mm
  expr: Constraints[14] = Sketch128.Constraints.length
  sketch-geometry (6):
    g0: ArcOfCircle CenterX=36.5 CenterY=-10 CenterZ=0 NormalX=0 NormalY=0 NormalZ=1 AngleXU=0 Radius=10 StartAngle=6.28318 EndAngle=7.85398
    g1: ArcOfCircle CenterX=-36.5 CenterY=-10 CenterZ=0 NormalX=0 NormalY=0 NormalZ=1 AngleXU=0 Radius=10 StartAngle=1.5708 EndAngle=3.14159
    g2: LineSegment StartX=-46.5 StartY=-10 StartZ=0 EndX=-46.5 EndY=0 EndZ=0
    g3: LineSegment StartX=-36.5 StartY=0 StartZ=0 EndX=-46.5 EndY=0 EndZ=0
    g4: LineSegment StartX=46.5 StartY=-10 StartZ=0 EndX=46.5 EndY=0 EndZ=0
    g5: LineSegment StartX=36.5 StartY=0 StartZ=0 EndX=46.5 EndY=0 EndZ=0
  constraints (17):
    c: PointOnObject(g0,g-1)
    c: PointOnObject(g1,g-1)
    c: Coincident(g2,g1)
    c: PointOnObject(g2,g-1)
    c: Vertical(g2)
    c: Tangent(g2,g1)
    c: Coincident(g3,g2)
    c: Coincident(g4,g0)
    c: PointOnObject(g4,g-1)
    c: Vertical(g4)
    c: Tangent(g4,g0)
    c: Coincident(g5,g4)
    c: Tangent(g5,g0) = 1.5708
    c: Tangent(g3,g1) = -1.5708
    c: DistanceX(g2,g4) = 93
    c: Symmetric(g1,g0,g-2)
    c: Diameter(g0) = 20
FEATURE [PartDesign::Mirrored] Mirrored040
  MirrorPlane = -> YZ_Plane001
FEATURE [PartDesign::PolarPattern] PolarPattern017
  Angle = 360
  Axis = -> Z_Axis001
  Occurrences = 3
FEATURE [PartDesign::CoordinateSystem] Local_CS042
  AttacherType = Attacher::AttachEngine3D
  AttachmentOffset = pos=(0,0,0) rot=(0,0,1;2.0944rad)
  MapMode = 5
  Placement = pos=(0,0,0) rot=(0,0,1;2.0944rad)
  Support = -> [XY_Plane001]
FEATURE [PartDesign::CoordinateSystem] Local_CS012
  AttacherType = Attacher::AttachEngine3D
  AttachmentOffset = pos=(16,119.5,157) rot=(0,0,-1;1.5708rad)
  MapMode = 5
  Placement = pos=(-111.49,-45.8936,157) rot=(0,0,1;0.523599rad)
  Support = -> [Local_CS042]
  expr: AttachmentOffset = Local_CS041.Placement
FEATURE [PartDesign::Plane] DatumPlane012
  Length = 594.137
  MapMode = 5
  Placement = pos=(-111.49,-45.8936,157) rot=(0,0,1;0.523599rad)
  ResizeMode = 0
  Support = -> [Local_CS012]
  Width = 579.207
FEATURE [PartDesign::Pocket] Pocket091
  BaseFeature = -> Pocket007
  Direction = (-0.5,-0.866025,-1e-16)
  Length = 16
  Length2 = 5
  Profile = -> Sketch134
  ReferenceAxis = -> Sketch134 [N_Axis]
  Refine = true
  Reversed = true
  Type = 0
  expr: Length = <<main>>.end_face_width / 2
FEATURE [Sketcher::SketchObject] Sketch136
  FullyConstrained = true
  MapMode = 5
  Support = -> [XY_Plane001]
  sketch-geometry (6):
    g0: LineSegment StartX=0 StartY=-100 StartZ=0 EndX=-86.6025 EndY=50 EndZ=0
    g1: LineSegment StartX=-86.6025 StartY=50 StartZ=0 EndX=86.6025 EndY=50 EndZ=0
    g2: LineSegment StartX=86.6025 StartY=50 StartZ=0 EndX=0 EndY=-100 EndZ=0
    g3: LineSegment StartX=-86.6025 StartY=50 StartZ=0 EndX=0 EndY=7.1e-15 EndZ=0
    g4: LineSegment StartX=0 StartY=7.1e-15 StartZ=0 EndX=86.6025 EndY=50 EndZ=0
    g5: LineSegment StartX=0 StartY=7.1e-15 StartZ=0 EndX=0 EndY=-100 EndZ=0
  constraints (15):
    c: PointOnObject(g0,g-2)
    c: Coincident(g1,g0)
    c: Horizontal(g1)
    c: Coincident(g2,g1)
    c: Coincident(g2,g0)
    c: Coincident(g3,g0)
    c: Coincident(g3,g-1)
    c: Coincident(g4,g3)
    c: Coincident(g4,g1)
    c: Coincident(g5,g3)
    c: Coincident(g5,g0)
    c: Equal(g3,g4)
    c: Equal(g4,g5)
    c: Equal(g0,g1)
    c: DistanceY(g1) = 50
FEATURE [PartDesign::Pocket] Pocket093
  BaseFeature = -> Pocket091
  Direction = (0,0,-1)
  Length = 157
  Length2 = 5
  Profile = -> Sketch136
  ReferenceAxis = -> Sketch136 [N_Axis]
  Reversed = true
  Type = 0
  expr: Length = <<main>>.basin_height
FEATURE [PartDesign::Pocket] Pocket083
  BaseFeature = -> Pocket093
  Direction = (0,0,-1)
  Length = 5
  Length2 = 5
  Midplane = true
  Profile = -> Sketch130
  ReferenceAxis = -> Sketch130 [N_Axis]
  Type = 1
FEATURE [PartDesign::MultiTransform] MultiTransform014
  BaseFeature = -> Pocket083
  Originals = -> [Pocket083]
  Transformations = -> [Mirrored040,PolarPattern017]
FEATURE [PartDesign::Pocket] Pocket082
  BaseFeature = -> MultiTransform014
  Direction = (0.5,-0.866025,-1e-16)
  Length = 33
  Length2 = 5
  Midplane = true
  Profile = -> Sketch129
  ReferenceAxis = -> Sketch129 [N_Axis]
  Type = 0
  expr: Length = <<main>>.end_face_width + 1mm
FEATURE [PartDesign::Pocket] Pocket006
  BaseFeature = -> Pocket082
  Direction = (-1,2e-16,-2e-16)
  Length = 33
  Length2 = 160
  Midplane = true
  Profile = -> Sketch009
  ReferenceAxis = -> Sketch009 [N_Axis]
  Type = 0
  expr: Length = <<main>>.end_face_width + 1mm
FEATURE [Sketcher::SketchObject] Sketch137
  AttachmentOffset = pos=(0,18.4752,0) rot=(0.935113,-0.250563,-0.250563;1.63783rad)
  ExternalGeometry = -> [Sketch128]
  FullyConstrained = true
  MapMode = 5
  Placement = pos=(-16,-9.2376,0) rot=(0.57735,0.57735,0.57735;2.0944rad)
  Support = -> [Local_CS042]
  expr: .AttachmentOffset.Base.y = -Sketch009.AttachmentOffset.Base.y
  expr: .AttachmentOffset.Rotation.Angle = Sketch009.AttachmentOffset.Rotation.Angle
  expr: .AttachmentOffset.Rotation.Axis = Sketch009.AttachmentOffset.Rotation.Axis
  expr: Constraints[20] = Sketch009.Constraints[20]
  expr: Constraints[21] = Sketch009.Constraints[21]
  expr: Constraints[34] = Sketch009.Constraints[34]
  expr: Constraints[35] = Sketch009.Constraints[35]
  expr: Constraints[7] = Sketch009.Constraints[7]
  sketch-geometry (18):
    g0: LineSegment StartX=0 StartY=0 StartZ=0 EndX=0 EndY=157 EndZ=0
    g1: LineSegment StartX=192.937 StartY=152 StartZ=0 EndX=192.937 EndY=127 EndZ=0
    g2: LineSegment StartX=187.937 StartY=122 StartZ=0 EndX=183.825 EndY=122 EndZ=0
    g3: LineSegment StartX=178.979 StartY=118.232 StartZ=0 EndX=148.93 EndY=0 EndZ=0
    g4: LineSegment StartX=148.93 StartY=0 StartZ=0 EndX=0 EndY=0 EndZ=0
    g5: ArcOfCircle CenterX=187.937 CenterY=152 CenterZ=0 NormalX=0 NormalY=0 NormalZ=1 AngleXU=0 Radius=5 StartAngle=2.5e-15 EndAngle=1.5708
    g6: GeomPoint X=192.937 Y=157 Z=0
    g7: ArcOfCircle CenterX=187.937 CenterY=127 CenterZ=0 NormalX=0 NormalY=0 NormalZ=1 AngleXU=0 Radius=5 StartAngle=4.71239 EndAngle=6.28319
    g8: GeomPoint X=192.937 Y=122 Z=0
    g9: ArcOfCircle CenterX=183.825 CenterY=117 CenterZ=0 NormalX=0 NormalY=0 NormalZ=1 AngleXU=0 Radius=5 StartAngle=1.5708 EndAngle=2.89271
    g10: GeomPoint X=179.937 Y=122 Z=0
    g11: LineSegment StartX=82.2376 StartY=116.5 StartZ=0 EndX=175.238 EndY=116.5 EndZ=0
    g12: LineSegment StartX=175.238 StartY=116.5 StartZ=0 EndX=175.238 EndY=157 EndZ=0
    g13: LineSegment StartX=175.238 StartY=157 StartZ=0 EndX=82.2376 EndY=157 EndZ=0
    g14: LineSegment StartX=82.2376 StartY=157 StartZ=0 EndX=82.2376 EndY=116.5 EndZ=0
    g15: LineSegment StartX=0 StartY=157 StartZ=0 EndX=82.2376 EndY=157 EndZ=0
    g16: LineSegment StartX=175.238 StartY=157 StartZ=0 EndX=187.937 EndY=157 EndZ=0
    g17: LineSegment StartX=208.395 StartY=149.752 StartZ=0 EndX=192.937 EndY=149.752 EndZ=0
  constraints (44):
    c: Coincident(g-1,g0)
    c: Vertical(g0)
    c: Vertical(g1)
    c: Horizontal(g2)
    c: PointOnObject(g3,g-1)
    c: Coincident(g3,g4)
    c: Coincident(g4,g0)
    c: DistanceY(g0,g0) = 157
    c: PointOnObject(g6,g1)
    c: Tangent(g1,g5) = 1.5708
    c: PointOnObject(g8,g2)
    c: PointOnObject(g8,g1)
    c: Tangent(g2,g7) = 1.5708
    c: Tangent(g1,g7) = 1.5708
    c: PointOnObject(g10,g3)
    c: PointOnObject(g10,g2)
    c: Tangent(g3,g9) = -1.5708
    c: Tangent(g2,g9) = -1.5708
    c: Equal(g9,g7)
    c: Equal(g7,g5)
    c: Diameter(g7) = 10
    c: Distance(g8,g10) = 13
    c: Coincident(g11,g12)
    c: Coincident(g12,g13)
    c: Coincident(g13,g14)
    c: Coincident(g14,g11)
    c: Coincident(g15,g0)
    c: Coincident(g15,g13)
    c: Coincident(g16,g12)
    c: Horizontal(g16)
    c: Tangent(g16,g5) = 1.5708
    c: PointOnObject(g6,g16)
    c: PointOnObject(g17,g1)
    c: Horizontal(g17)
    c: DistanceX(g17) = 208.395
    c: DistanceY(g17) = 149.752
    c: Coincident(g11,g-3)
    c: Angle(g3,g-1) = 1.81968
    c: Distance(g11,g3) = 3.2
    c: DistanceY(g8,g14) = 35
    c: Coincident(g11,g-4)
    c: Perpendicular(g12,g13)
    c: Perpendicular(g14,g11)
    c: Coincident(g12,g-5)
FEATURE [PartDesign::Pocket] Pocket094
  BaseFeature = -> Pocket006
  Direction = (-1,1e-16,-4e-16)
  Length = 5
  Length2 = 5
  Profile = -> Sketch137
  ReferenceAxis = -> Sketch137 [N_Axis]
  Reversed = true
  Type = 0
FEATURE [PartDesign::Mirrored] Mirrored002
  BaseFeature = -> Pocket094
  MirrorPlane = -> DatumPlane014
  Originals = -> [Pocket006,Pocket094]
FEATURE [PartDesign::Body] Body001  label="Body001_material_0.30ansi"
  Group = -> [Local_CS,Local_CS011,Sketch003,BaseBend001,Local_CS012,DatumPlane011,DatumPlane012,Local_CS035,Local_CS036,Local_CS037,Local_CS038,Sketch112,Sketch113,Sketch128,Pocket081,Local_CS039,PolarPattern016,Bend,Pocket007,Pocket091,Sketch129,Local_CS041,Sketch130,Sketch136,Pocket093,Pocket083,MultiTransform014,Mirrored040,PolarPattern017,Local_CS042,Pocket082,Pocket006,Sketch137,Pocket094,Mirrored002,+58 more]
  Origin = -> Origin001
  Tip = -> Pocket094
COMPONENT P2 — geometry summary ("module001"; no construction recipe available for this part):
  bounding box: 170.0 x 148.0 x 41.1 mm
  tessellated surface: 7,996 triangles
  volume: 46706 mm^3 (5% of its bounding box)
  symmetry: mirror-symmetric across its y mid-plane
COMPONENT P3 — recipe-attached ("basin_cover", modeled in this document).
Construction recipe (the document's own serialized feature program — sketch geometry with constraints, then the solid features built on it; lengths are millimeters unless a unit is written):

FEATURE [Sketcher::SketchObject] Sketch047
  FullyConstrained = true
  MapMode = 5
  Support = -> [XY_Plane015]
  expr: Constraints[16] = Sketch003.Constraints.max_r
  expr: Constraints[20] = <<main>>.work_plane_width
  sketch-geometry (8):
    g0: ArcOfCircle CenterX=0 CenterY=18.4752 CenterZ=0 NormalX=0 NormalY=0 NormalZ=1 AngleXU=0 Radius=60 StartAngle=0.539993 EndAngle=1.5708
    g1: ArcOfCircle CenterX=52.3205 CenterY=49.8371 CenterZ=0 NormalX=0 NormalY=0 NormalZ=1 AngleXU=0 Radius=1 StartAngle=3.68159 EndAngle=5.23599
    g2: LineSegment StartX=52.8205 StartY=48.9711 StartZ=0 EndX=172.268 EndY=117.934 EndZ=0
    g3: ArcOfCircle CenterX=171.768 CenterY=118.8 CenterZ=0 NormalX=0 NormalY=0 NormalZ=1 AngleXU=0 Radius=1 StartAngle=5.23599 EndAngle=6.88827
    g4: ArcOfCircle CenterX=0 CenterY=0 CenterZ=0 NormalX=0 NormalY=0 NormalZ=1 AngleXU=0 Radius=209.848 StartAngle=0.605088 EndAngle=1.5708
    g5: LineSegment StartX=3.7e-15 StartY=78.4752 StartZ=0 EndX=1.28e-14 EndY=209.848 EndZ=0
    g6: LineSegment StartX=52.8205 StartY=48.9711 StartZ=0 EndX=0 EndY=18.4752 EndZ=0
    g7: GeomPoint X=173.205 Y=118.475 Z=0
  constraints (22):
    c: PointOnObject(g0,g-2)
    c: PointOnObject(g4,g-2)
    c: Diameter(g1) = 2
    c: Diameter(g3) = 2
    c: Tangent(g1,g0) = 1.5708
    c: Tangent(g3,g2) = -1.5708
    c: Angle(g2,g-1) = 2.61799
    c: Coincident(g5,g0)
    c: Coincident(g5,g4)
    c: Tangent(g1,g2) = -1.5708
    c: Coincident(g6,g1)
    c: Tangent(g6,g2)
    c: Coincident(g6,g0)
    c: Diameter(g0) = 120
    c: PointOnObject(g7,g4)
    c: PointOnObject(g7,g2)
    c: DistanceY(g4) = 209.848
    c: Distance(g4,g0) = 18.4752  'major_r_offset'
    c: Coincident(g4,g-1)
    c: PointOnObject(g0,g-2)
    c: Distance(g0,g7) = 200
    c: Tangent(g3,g4) = -1.5708
FEATURE [PartDesign::Pad] Pad012
  Direction = (0,0,1)
  Length = 3
  Length2 = 10
  Profile = -> Sketch047
  ReferenceAxis = -> Sketch047 [N_Axis]
  Type = 0
FEATURE [PartDesign::CoordinateSystem] Local_CS013
  AttacherType = Attacher::AttachEngine3D
  MapMode = 5
  Support = -> [XY_Plane015]
FEATURE [PartDesign::CoordinateSystem] Local_CS016
  AttacherType = Attacher::AttachEngine3D
  AttachmentOffset = pos=(0,0,0) rot=(0,0,1;0.523599rad)
  MapMode = 5
  Placement = pos=(0,0,0) rot=(0,0,1;0.523599rad)
  Support = -> [XY_Plane015]
FEATURE [PartDesign::Plane] DatumPlane015
  Length = 495.835
  MapMode = 5
  Placement = pos=(0,0,0) rot=(0,0,1;0.523599rad)
  ResizeMode = 0
  Support = -> [Local_CS016]
  Width = 455.324
FEATURE [PartDesign::Plane] DatumPlane016
  Length = 79.989
  MapMode = 4
  Placement = pos=(86.82,84.1932,0) rot=(0.377964,0.654654,0.654654;2.41886rad)
  ResizeMode = 0
  Width = 61.6877
FEATURE [PartDesign::CoordinateSystem] Local_CS026
  AttacherType = Attacher::AttachEngine3D
  AttachmentOffset = pos=(0,18.4752,0) rot=(0,0,1;0.523599rad)
  MapMode = 5
  Placement = pos=(0,18.4752,0) rot=(0,0,1;0.523599rad)
  Support = -> [XY_Plane015]
  expr: .AttachmentOffset.Base.y = Sketch047.Constraints.major_r_offset
FEATURE [PartDesign::SubShapeBinder] Binder041
  BindCopyOnChange = 0
  BindMode = 0
  ClaimChildren = false
  Context = -> Model [Body001003005002.Binder041.]
  Fuse = false
  MakeFace = true
  OffsetFill = false
  OffsetIntersection = false
  OffsetJoinType = 0
  OffsetOpenResult = false
  PartialLoad = false
  Relative = false
  Support = -> [Body001003005003013[Pocket041.Sketch083.]]
  _Version = 2
FEATURE [PartDesign::SubShapeBinder] Binder042
  BindCopyOnChange = 0
  BindMode = 0
  ClaimChildren = false
  Context = -> Model [Body001003005002.Binder042.]
  Fuse = false
  MakeFace = true
  OffsetFill = false
  OffsetIntersection = false
  OffsetJoinType = 0
  OffsetOpenResult = false
  PartialLoad = false
  Relative = false
  Support = -> [Body001003005003013[Pocket042.Sketch084.]]
  _Version = 2
FEATURE [PartDesign::SubShapeBinder] Binder043
  BindCopyOnChange = 0
  BindMode = 0
  ClaimChildren = false
  Context = -> Model [Body001003005002.Binder043.]
  Fuse = false
  MakeFace = true
  OffsetFill = false
  OffsetIntersection = false
  OffsetJoinType = 0
  OffsetOpenResult = false
  PartialLoad = false
  Placement = pos=(88.49,85.7308,0) rot=(0,0,1;0.523599rad)
  Relative = false
  Support = -> [Body001[Sketch043.]]
  _Version = 2
  expr: Placement = Local_CS043.Placement
FEATURE [PartDesign::CoordinateSystem] Local_CS043
  AttacherType = Attacher::AttachEngine3D
  AttachmentOffset = pos=(119.5,30,0) rot=(0,0,1;0rad)
  MapMode = 5
  Placement = pos=(88.49,85.7308,0) rot=(0,0,1;0.523599rad)
  Support = -> [Local_CS016]
  expr: .AttachmentOffset.Base.x = Local_CS012.AttachmentOffset.Base.y
FEATURE [PartDesign::Pocket] Pocket086
  BaseFeature = -> Pad012
  Direction = (0,0,-1)
  Length = 5
  Length2 = 5
  Midplane = true
  Profile = -> Binder043
  Type = 1
FEATURE [PartDesign::CoordinateSystem] Local_CS044
  AttacherType = Attacher::AttachEngine3D
  AttachmentOffset = pos=(119.5,13,0) rot=(0,0,1;0rad)
  MapMode = 5
  Placement = pos=(96.99,71.0083,0) rot=(0,0,1;0.523599rad)
  Support = -> [Local_CS016]
  expr: .AttachmentOffset.Base.x = Local_CS043.AttachmentOffset.Base.x
  expr: .AttachmentOffset.Base.y = <<main>>.end_face_width / 2 - <<main>>.thickness
FEATURE [PartDesign::SubShapeBinder] Binder046
  BindCopyOnChange = 0
  BindMode = 0
  ClaimChildren = false
  Context = -> Model [Body001003005002.Binder046.]
  Fuse = false
  MakeFace = true
  OffsetFill = false
  OffsetIntersection = false
  OffsetJoinType = 0
  OffsetOpenResult = false
  PartialLoad = false
  Placement = pos=(96.99,71.0083,0) rot=(0,0,1;0.523599rad)
  Relative = false
  Support = -> [Body001[Pocket073.Sketch073.]]
  _Version = 2
  expr: Placement = Local_CS044.Placement
FEATURE [PartDesign::Pocket] Pocket089
  BaseFeature = -> Pocket086
  Direction = (0,0,-1)
  Length = 5
  Length2 = 5
  Midplane = true
  Profile = -> Binder046
  Type = 1
FEATURE [PartDesign::Mirrored] Mirrored014
  BaseFeature = -> Pocket089
  MirrorPlane = -> Sketch047 [V_Axis]
  Originals = -> [Pad012,Pocket086,Pocket089]
  Refine = true
FEATURE [PartDesign::Pocket] Pocket084
  BaseFeature = -> Mirrored014
  Direction = (0,0,-1)
  Length = 5
  Length2 = 5
  Midplane = true
  Profile = -> Binder041
  Type = 1
FEATURE [PartDesign::Pocket] Pocket085
  BaseFeature = -> Pocket084
  Direction = (0,0,-1)
  Length = 5
  Length2 = 5
  Midplane = true
  Profile = -> Binder042
  Type = 1
FEATURE [PartDesign::Body] Body001003005  label="basin_cover"
  Group = -> [Sketch047,Pad012,Pocket086,Pocket089,Mirrored014,Local_CS013,Local_CS016,DatumPlane015,DatumPlane016,Local_CS026,Binder041,Binder042,Pocket084,Pocket085,Binder043,Local_CS043,Local_CS044,Binder046]
  Origin = -> Origin014
  Placement = pos=(0,0,0) rot=(0,0,1;1.0472rad)
  Tip = -> Pocket085
COMPONENT P4 — recipe-attached ("basement", modeled in this document).
Construction recipe (the document's own serialized feature program — sketch geometry with constraints, then the solid features built on it; lengths are millimeters unless a unit is written):

FEATURE [Sketcher::SketchObject] Sketch048
  FullyConstrained = true
  MapMode = 5
  Support = -> [XY_Plane016]
  expr: Constraints[1] = Sketch003.Constraints.max_r + 2.5mm
  sketch-geometry (1):
    g0: Circle CenterX=0 CenterY=0 CenterZ=0 NormalX=0 NormalY=0 NormalZ=1 AngleXU=0 Radius=212.348
  constraints (2):
    c: Coincident(g0,g-1)
    c: Radius(g0) = 212.348
FEATURE [PartDesign::Pad] Pad013
  Direction = (0,0,1)
  Length = 3
  Length2 = 10
  Profile = -> Sketch048
  ReferenceAxis = -> Sketch048 [N_Axis]
  Type = 0
  expr: Length = <<main>>.thickness
FEATURE [Sketcher::SketchObject] Sketch049
  AttachmentOffset = pos=(0,196.563,0) rot=(0,0,1;0rad)
  FullyConstrained = true
  MapMode = 5
  Placement = pos=(0,196.563,0) rot=(0,0,1;0rad)
  Support = -> [XY_Plane016]
  expr: .AttachmentOffset.Base.y = Sketch003.Constraints.total_petal_length - .Constraints.cut_width / 2 - 3.175mm - <<main>>.thickness
  expr: Constraints[10] = <<main>>.inner_width / 2
  expr: Constraints[14] = -<<main>>.inner_width / 2
  sketch-geometry (9):
    g0: ArcOfCircle CenterX=-13 CenterY=8.0875 CenterZ=0 NormalX=0 NormalY=0 NormalZ=1 AngleXU=0 Radius=1.5875 StartAngle=1.5708 EndAngle=4.71239
    g1: LineSegment StartX=-13 StartY=6.5 StartZ=0 EndX=9.825 EndY=6.5 EndZ=0
    g2: LineSegment StartX=9.825 StartY=6.5 StartZ=0 EndX=9.825 EndY=0 EndZ=0
    g3: LineSegment StartX=9.825 StartY=0 StartZ=0 EndX=13 EndY=0 EndZ=0
    g4: LineSegment StartX=13 StartY=0 StartZ=0 EndX=13 EndY=6.5 EndZ=0
    g5: LineSegment StartX=-13 StartY=9.675 StartZ=0 EndX=9.825 EndY=9.675 EndZ=0
    g6: ArcOfCircle CenterX=9.825 CenterY=6.5 CenterZ=0 NormalX=0 NormalY=0 NormalZ=1 AngleXU=0 Radius=3.175 StartAngle=1.117e-13 EndAngle=1.5708
    g7: GeomPoint X=9.825 Y=-6.5 Z=0
    g8: GeomPoint X=9.825 Y=-9.675 Z=0
  constraints (21):
    c: Horizontal(g1)
    c: PointOnObject(g2,g-1)
    c: Vertical(g2)
    c: Coincident(g3,g2)
    c: PointOnObject(g3,g-1)
    c: Coincident(g4,g3)
    c: Vertical(g4)
    c: Horizontal(g5)
    c: Tangent(g6,g4) = -1.5708
    c: Tangent(g6,g5) = 1.5708
    c: DistanceX(g3) = 13
    c: Tangent(g1,g0) = -1.5708
    c: Tangent(g5,g0) = 1.5708
    c: Diameter(g0) = 3.175
    c: DistanceX(g0) = -13
    c: Coincident(g6,g2)
    c: Coincident(g2,g1)
    c: Symmetric(g7,g1,g2)
    c: DistanceY(g7,g1) = 13  'cut_width'
    c: Symmetric(g8,g5,g2)
    c: DistanceY(g8,g5) = 19.35  'total_width'
FEATURE [Sketcher::SketchObject] Sketch050
  AttachmentOffset = pos=(0,196.563,0) rot=(0,0,1;0rad)
  FullyConstrained = true
  MapMode = 5
  Placement = pos=(0,196.563,0) rot=(0,0,1;0rad)
  Support = -> [XY_Plane016]
  expr: .AttachmentOffset.Base.y = Sketch049.AttachmentOffset.Base.y
  expr: .Constraints.cut_width = Sketch049.Constraints[18]
  expr: Constraints[10] = Sketch049.Constraints[10]
  expr: Constraints[13] = Sketch049.Constraints[13]
  expr: Constraints[14] = Sketch049.Constraints[14]
  expr: Constraints[29] = Sketch049.Constraints[10]
  expr: Constraints[32] = Sketch049.Constraints[13]
  expr: Constraints[33] = Sketch049.Constraints[14]
  sketch-geometry (17):
    g0: LineSegment StartX=-13 StartY=-8.0875 StartZ=0 EndX=-13 EndY=8.0875 EndZ=0
    g1: ArcOfCircle CenterX=-13 CenterY=8.0875 CenterZ=0 NormalX=0 NormalY=0 NormalZ=1 AngleXU=0 Radius=1.5875 StartAngle=1.5708 EndAngle=4.71239
    g2: LineSegment StartX=-13 StartY=6.5 StartZ=0 EndX=9.825 EndY=6.5 EndZ=0
    g3: LineSegment StartX=9.825 StartY=6.5 StartZ=0 EndX=9.825 EndY=0 EndZ=0
    g4: LineSegment StartX=9.825 StartY=0 StartZ=0 EndX=13 EndY=0 EndZ=0
    g5: LineSegment StartX=13 StartY=0 StartZ=0 EndX=13 EndY=6.5 EndZ=0
    g6: LineSegment StartX=-13 StartY=9.675 StartZ=0 EndX=9.825 EndY=9.675 EndZ=0
    g7: ArcOfCircle CenterX=9.825 CenterY=6.5 CenterZ=0 NormalX=0 NormalY=0 NormalZ=1 AngleXU=0 Radius=3.175 StartAngle=1.742e-13 EndAngle=1.5708
    g8: GeomPoint X=9.825 Y=-6.5 Z=0
    g9: ArcOfCircle CenterX=-11.5 CenterY=11.5875 CenterZ=0 NormalX=0 NormalY=0 NormalZ=1 AngleXU=0 Radius=1.5875 StartAngle=1.5708 EndAngle=4.71239
    g10: LineSegment StartX=-11.5 StartY=10 StartZ=0 EndX=9.825 EndY=10 EndZ=0
    g11: LineSegment StartX=9.825 StartY=10 StartZ=0 EndX=9.825 EndY=0 EndZ=0
    g12: LineSegment StartX=9.825 StartY=0 StartZ=0 EndX=13 EndY=0 EndZ=0
    g13: LineSegment StartX=13 StartY=0 StartZ=0 EndX=13 EndY=10 EndZ=0
    g14: LineSegment StartX=-11.5 StartY=13.175 StartZ=0 EndX=9.825 EndY=13.175 EndZ=0
    g15: ArcOfCircle CenterX=9.825 CenterY=10 CenterZ=0 NormalX=0 NormalY=0 NormalZ=1 AngleXU=0 Radius=3.175 StartAngle=1e-16 EndAngle=1.5708
    g16: GeomPoint X=9.825 Y=-10 Z=0
  constraints (40):
    c: Horizontal(g2)
    c: PointOnObject(g3,g-1)
    c: Vertical(g3)
    c: Coincident(g4,g3)
    c: PointOnObject(g4,g-1)
    c: Coincident(g5,g4)
    c: Vertical(g5)
    c: Horizontal(g6)
    c: Tangent(g7,g5) = -1.5708
    c: Tangent(g7,g6) = 1.5708
    c: DistanceX(g4) = 13
    c: Tangent(g2,g1) = -1.5708
    c: Tangent(g6,g1) = 1.5708
    c: Diameter(g1) = 3.175
    c: DistanceX(g1) = -13
    c: Coincident(g7,g3)
    c: Coincident(g3,g2)
    c: Symmetric(g8,g2,g3)
    c: DistanceY(g8,g2) = 13  'cut_width'
    c: Horizontal(g10)
    c: PointOnObject(g11,g-1)
    c: Vertical(g11)
    c: Coincident(g12,g11)
    c: PointOnObject(g12,g-1)
    c: Coincident(g13,g12)
    c: Vertical(g13)
    c: Horizontal(g14)
    c: Tangent(g15,g13) = -1.5708
    c: Tangent(g15,g14) = 1.5708
    c: DistanceX(g12) = 13
    c: Tangent(g10,g9) = -1.5708
    c: Tangent(g14,g9) = 1.5708
    c: Diameter(g9) = 3.175
    c: DistanceX(g9) = -11.5
    c: Coincident(g15,g11)
    c: Coincident(g11,g10)
    c: Symmetric(g16,g10,g11)
    c: DistanceY(g16,g10) = 20  'cut_width'
    c: Coincident(g0,g1)
    c: Symmetric(g0,g0,g-1)
FEATURE [PartDesign::CoordinateSystem] Local_CS017
  AttacherType = Attacher::AttachEngine3D
  AttachmentOffset = pos=(0,0,3) rot=(0,0,1;0rad)
  MapMode = 5
  Placement = pos=(0,0,3) rot=(0,0,1;0rad)
  Support = -> [XY_Plane016]
  expr: .AttachmentOffset.Base.z = <<main>>.thickness
FEATURE [PartDesign::SubShapeBinder] Binder004
  AttacherType = Attacher::AttachEngine3D
  AttachmentOffset = pos=(0,196.563,0) rot=(0,0,1;3.14159rad)
  BindCopyOnChange = 0
  BindMode = 0
  ClaimChildren = false
  Context = -> Model [Body001003005003002.Binder004.]
  Fuse = false
  MakeFace = true
  MapMode = 5
  OffsetFill = false
  OffsetIntersection = false
  OffsetJoinType = 0
  OffsetOpenResult = false
  PartialLoad = false
  Placement = pos=(0,180.388,0) rot=(0,0,1;3.14159rad)
  Relative = false
  _Version = 2
  expr: .AttachmentOffset.Base.y = <<main>>.work_plane_width + Sketch003.Constraints.petal_offset - <<main>>.thickness - 3.175mm - Sketch049.Constraints.cut_width / 2
  expr: .Placement.Base.y = Sketch049.AttachmentOffset.Base.y - Sketch049.Constraints.cut_width - 3.175mm
FEATURE [PartDesign::Plane] DatumPlane017
  Length = 453.129
  MapMode = 3
  Placement = pos=(0,180.388,0) rot=(0,0.707107,0.707107;3.14159rad)
  ResizeMode = 0
  Support = -> [Binder004]
  Width = 79.1207
FEATURE [Sketcher::SketchObject] Sketch051
  AttachmentOffset = pos=(0,180.388,0) rot=(0,0,1;0rad)
  FullyConstrained = true
  MapMode = 5
  Placement = pos=(0,180.388,0) rot=(0,0,1;0rad)
  Support = -> [XY_Plane016]
  expr: .AttachmentOffset.Base.y = Binder004.Placement.Base.y
  expr: .Constraints.cut_width = Sketch049.Constraints[18]
  expr: Constraints[10] = Sketch049.Constraints[10]
  expr: Constraints[13] = Sketch049.Constraints[13]
  expr: Constraints[14] = Sketch049.Constraints[14]
  sketch-geometry (9):
    g0: ArcOfCircle CenterX=-11.5 CenterY=8.0875 CenterZ=0 NormalX=0 NormalY=0 NormalZ=1 AngleXU=0 Radius=1.5875 StartAngle=1.5708 EndAngle=4.71239
    g1: LineSegment StartX=-11.5 StartY=6.5 StartZ=0 EndX=9.825 EndY=6.5 EndZ=0
    g2: LineSegment StartX=9.825 StartY=6.5 StartZ=0 EndX=9.825 EndY=0 EndZ=0
    g3: LineSegment StartX=9.825 StartY=0 StartZ=0 EndX=13 EndY=0 EndZ=0
    g4: LineSegment StartX=13 StartY=0 StartZ=0 EndX=13 EndY=6.5 EndZ=0
    g5: LineSegment StartX=-11.5 StartY=9.675 StartZ=0 EndX=9.825 EndY=9.675 EndZ=0
    g6: ArcOfCircle CenterX=9.825 CenterY=6.5 CenterZ=0 NormalX=0 NormalY=0 NormalZ=1 AngleXU=0 Radius=3.175 StartAngle=0 EndAngle=1.5708
    g7: GeomPoint X=9.825 Y=-6.5 Z=0
    g8: LineSegment StartX=11.5 StartY=8.0875 StartZ=0 EndX=11.5 EndY=-8.0875 EndZ=0
  constraints (22):
    c: Horizontal(g1)
    c: PointOnObject(g2,g-1)
    c: Vertical(g2)
    c: Coincident(g3,g2)
    c: PointOnObject(g3,g-1)
    c: Coincident(g4,g3)
    c: Vertical(g4)
    c: Horizontal(g5)
    c: Tangent(g6,g4) = -1.5708
    c: Tangent(g6,g5) = 1.5708
    c: DistanceX(g3) = 13
    c: Tangent(g1,g0) = -1.5708
    c: Tangent(g5,g0) = 1.5708
    c: Diameter(g0) = 3.175
    c: DistanceX(g0) = -11.5
    c: Coincident(g6,g2)
    c: Coincident(g2,g1)
    c: Symmetric(g7,g1,g2)
    c: DistanceY(g7,g1) = 13  'cut_width'
    c: Vertical(g8)
    c: Symmetric(g0,g8,g-1)
    c: Horizontal(g8,g0)
FEATURE [PartDesign::SubShapeBinder] Binder005
  AttacherType = Attacher::AttachEngine3D
  AttachmentOffset = pos=(0,0,0) rot=(0,0,1;1.0472rad)
  BindCopyOnChange = 0
  BindMode = 0
  ClaimChildren = false
  Context = -> Body001003005003 [Binder005.]
  Fuse = false
  MakeFace = true
  MapMode = 5
  OffsetFill = false
  OffsetIntersection = false
  OffsetJoinType = 0
  OffsetOpenResult = false
  PartialLoad = false
  Placement = pos=(0,0,0) rot=(0,0,1;1.0472rad)
  Relative = false
  _Version = 2
FEATURE [PartDesign::Plane] DatumPlane018
  Length = 613.419
  MapMode = 4
  Placement = pos=(0,0,0) rot=(0.186157,0.694747,0.694747;2.77349rad)
  ResizeMode = 0
  Support = -> [Binder005]
  Width = 84.0405
FEATURE [Sketcher::SketchObject] Sketch057
  AttachmentOffset = pos=(196.563,-11.5,0) rot=(0,0,1;0rad)
  FullyConstrained = true
  MapMode = 5
  Placement = pos=(4.62e-14,196.563,-11.5) rot=(0.57735,0.57735,0.57735;2.0944rad)
  Support = -> [YZ_Plane015]
  expr: .AttachmentOffset.Base.x = Sketch049.AttachmentOffset.Base.y
  expr: .AttachmentOffset.Base.y = -23mm / 2
  expr: Constraints[1] = <<main>>.rivet_d
  sketch-geometry (1):
    g0: Circle CenterX=0 CenterY=0 CenterZ=0 NormalX=0 NormalY=0 NormalZ=1 AngleXU=0 Radius=1.7
  constraints (2):
    c: Coincident(g0,g-1)
    c: Diameter(g0) = 3.4
FEATURE [Sketcher::SketchObject] Sketch058
  AttachmentOffset = pos=(180.388,-11.5,0) rot=(0,0,1;0rad)
  FullyConstrained = true
  MapMode = 5
  Placement = pos=(4.26e-14,180.388,-11.5) rot=(0.57735,0.57735,0.57735;2.0944rad)
  Support = -> [YZ_Plane015]
  expr: .AttachmentOffset.Base.x = Binder004.Placement.Base.y
  expr: .AttachmentOffset.Base.y = Sketch057.AttachmentOffset.Base.y
  expr: Constraints[1] = <<main>>.rivet_d
  sketch-geometry (1):
    g0: Circle CenterX=0 CenterY=0 CenterZ=0 NormalX=0 NormalY=0 NormalZ=1 AngleXU=0 Radius=1.7
  constraints (2):
    c: Coincident(g0,g-1)
    c: Diameter(g0) = 3.4
FEATURE [PartDesign::Pocket] Pocket027
  BaseFeature = -> Pad013
  Direction = (-1,2e-16,-3e-16)
  Length = 5
  Length2 = 5
  Midplane = true
  Profile = -> Sketch058
  ReferenceAxis = -> Sketch058 [N_Axis]
  Type = 1
FEATURE [PartDesign::CoordinateSystem] Local_CS021
  AttacherType = Attacher::AttachEngine3D
  AttachmentOffset = pos=(0,0,0) rot=(0,0,1;2.0944rad)
  MapMode = 5
  Placement = pos=(0,0,0) rot=(0,0,1;2.0944rad)
  Support = -> [XY_Plane016]
FEATURE [PartDesign::CoordinateSystem] Local_CS022
  AttacherType = Attacher::AttachEngine3D
  AttachmentOffset = pos=(0,0,0) rot=(0,0,-1;2.0944rad)
  MapMode = 5
  Placement = pos=(0,0,0) rot=(0,0,-1;2.0944rad)
  Support = -> [XY_Plane016]
FEATURE [PartDesign::Plane] DatumPlane019
  Length = 695.392
  MapMode = 5
  Placement = pos=(0,0,0) rot=(0,0,1;2.0944rad)
  ResizeMode = 0
  Support = -> [Local_CS021]
  Width = 695.266
FEATURE [PartDesign::Plane] DatumPlane020
  Length = 695.392
  MapMode = 5
  Placement = pos=(0,0,0) rot=(0,0,-1;2.0944rad)
  ResizeMode = 0
  Support = -> [Local_CS022]
  Width = 695.266
FEATURE [Sketcher::SketchObject] Sketch061
  AttachmentOffset = pos=(0,196.563,0) rot=(0,0,1;0rad)
  FullyConstrained = true
  MapMode = 5
  Placement = pos=(-170.228,-98.2813,0) rot=(0,0,1;2.0944rad)
  Support = -> [DatumPlane019]
  expr: .AttachmentOffset.Base.y = Sketch050.Placement.Base.y
  expr: .Constraints.cut_width = 13
  expr: Constraints[10] = Sketch050.Constraints[10]
  expr: Constraints[13] = Sketch050.Constraints[13]
  expr: Constraints[14] = Sketch050.Constraints[14]
  expr: Constraints[29] = Sketch050.Constraints[29]
  expr: Constraints[32] = Sketch050.Constraints[32]
  expr: Constraints[33] = Sketch050.Constraints[33]
  sketch-geometry (17):
    g0: LineSegment StartX=-13 StartY=-8.0875 StartZ=0 EndX=-13 EndY=8.0875 EndZ=0
    g1: ArcOfCircle CenterX=-13 CenterY=8.0875 CenterZ=0 NormalX=0 NormalY=0 NormalZ=1 AngleXU=0 Radius=1.5875 StartAngle=1.5708 EndAngle=4.71239
    g2: LineSegment StartX=-13 StartY=6.5 StartZ=0 EndX=9.825 EndY=6.5 EndZ=0
    g3: LineSegment StartX=9.825 StartY=6.5 StartZ=0 EndX=9.825 EndY=0 EndZ=0
    g4: LineSegment StartX=9.825 StartY=0 StartZ=0 EndX=13 EndY=0 EndZ=0
    g5: LineSegment StartX=13 StartY=0 StartZ=0 EndX=13 EndY=6.5 EndZ=0
    g6: LineSegment StartX=-13 StartY=9.675 StartZ=0 EndX=9.825 EndY=9.675 EndZ=0
    g7: ArcOfCircle CenterX=9.825 CenterY=6.5 CenterZ=0 NormalX=0 NormalY=0 NormalZ=1 AngleXU=0 Radius=3.175 StartAngle=1.743e-13 EndAngle=1.5708
    g8: GeomPoint X=9.825 Y=-6.5 Z=0
    g9: ArcOfCircle CenterX=-11.5 CenterY=11.5875 CenterZ=0 NormalX=0 NormalY=0 NormalZ=1 AngleXU=0 Radius=1.5875 StartAngle=1.5708 EndAngle=4.71239
    g10: LineSegment StartX=-11.5 StartY=10 StartZ=0 EndX=9.825 EndY=10 EndZ=0
    g11: LineSegment StartX=9.825 StartY=10 StartZ=0 EndX=9.825 EndY=0 EndZ=0
    g12: LineSegment StartX=9.825 StartY=0 StartZ=0 EndX=13 EndY=0 EndZ=0
    g13: LineSegment StartX=13 StartY=0 StartZ=0 EndX=13 EndY=10 EndZ=0
    g14: LineSegment StartX=-11.5 StartY=13.175 StartZ=0 EndX=9.825 EndY=13.175 EndZ=0
    g15: ArcOfCircle CenterX=9.825 CenterY=10 CenterZ=0 NormalX=0 NormalY=0 NormalZ=1 AngleXU=0 Radius=3.175 StartAngle=1e-16 EndAngle=1.5708
    g16: GeomPoint X=9.825 Y=-10 Z=0
  constraints (40):
    c: Horizontal(g2)
    c: PointOnObject(g3,g-1)
    c: Vertical(g3)
    c: Coincident(g4,g3)
    c: PointOnObject(g4,g-1)
    c: Coincident(g5,g4)
    c: Vertical(g5)
    c: Horizontal(g6)
    c: Tangent(g7,g5) = -1.5708
    c: Tangent(g7,g6) = 1.5708
    c: DistanceX(g4) = 13
    c: Tangent(g2,g1) = -1.5708
    c: Tangent(g6,g1) = 1.5708
    c: Diameter(g1) = 3.175
    c: DistanceX(g1) = -13
    c: Coincident(g7,g3)
    c: Coincident(g3,g2)
    c: Symmetric(g8,g2,g3)
    c: DistanceY(g8,g2) = 13  'cut_width'
    c: Horizontal(g10)
    c: PointOnObject(g11,g-1)
    c: Vertical(g11)
    c: Coincident(g12,g11)
    c: PointOnObject(g12,g-1)
    c: Coincident(g13,g12)
    c: Vertical(g13)
    c: Horizontal(g14)
    c: Tangent(g15,g13) = -1.5708
    c: Tangent(g15,g14) = 1.5708
    c: DistanceX(g12) = 13
    c: Tangent(g10,g9) = -1.5708
    c: Tangent(g14,g9) = 1.5708
    c: Diameter(g9) = 3.175
    c: DistanceX(g9) = -11.5
    c: Coincident(g15,g11)
    c: Coincident(g11,g10)
    c: Symmetric(g16,g10,g11)
    c: DistanceY(g16,g10) = 20  'cut_width'
    c: Coincident(g0,g1)
    c: Symmetric(g0,g0,g-1)
FEATURE [Sketcher::SketchObject] Sketch062
  AttachmentOffset = pos=(0,196.563,0) rot=(0,0,1;0rad)
  FullyConstrained = true
  MapMode = 5
  Placement = pos=(170.228,-98.2813,0) rot=(0,0,-1;2.0944rad)
  Support = -> [DatumPlane020]
  expr: .Constraints.cut_width = 13
  expr: AttachmentOffset = Sketch050.AttachmentOffset
  expr: Constraints[10] = Sketch050.Constraints[10]
  expr: Constraints[13] = Sketch050.Constraints[13]
  expr: Constraints[14] = Sketch050.Constraints[14]
  expr: Constraints[29] = Sketch050.Constraints[29]
  expr: Constraints[32] = Sketch050.Constraints[32]
  expr: Constraints[33] = Sketch050.Constraints[33]
  sketch-geometry (17):
    g0: LineSegment StartX=-13 StartY=-8.0875 StartZ=0 EndX=-13 EndY=8.0875 EndZ=0
    g1: ArcOfCircle CenterX=-13 CenterY=8.0875 CenterZ=0 NormalX=0 NormalY=0 NormalZ=1 AngleXU=0 Radius=1.5875 StartAngle=1.5708 EndAngle=4.71239
    g2: LineSegment StartX=-13 StartY=6.5 StartZ=0 EndX=9.825 EndY=6.5 EndZ=0
    g3: LineSegment StartX=9.825 StartY=6.5 StartZ=0 EndX=9.825 EndY=0 EndZ=0
    g4: LineSegment StartX=9.825 StartY=0 StartZ=0 EndX=13 EndY=0 EndZ=0
    g5: LineSegment StartX=13 StartY=0 StartZ=0 EndX=13 EndY=6.5 EndZ=0
    g6: LineSegment StartX=-13 StartY=9.675 StartZ=0 EndX=9.825 EndY=9.675 EndZ=0
    g7: ArcOfCircle CenterX=9.825 CenterY=6.5 CenterZ=0 NormalX=0 NormalY=0 NormalZ=1 AngleXU=0 Radius=3.175 StartAngle=1.743e-13 EndAngle=1.5708
    g8: GeomPoint X=9.825 Y=-6.5 Z=0
    g9: ArcOfCircle CenterX=-11.5 CenterY=11.5875 CenterZ=0 NormalX=0 NormalY=0 NormalZ=1 AngleXU=0 Radius=1.5875 StartAngle=1.5708 EndAngle=4.71239
    g10: LineSegment StartX=-11.5 StartY=10 StartZ=0 EndX=9.825 EndY=10 EndZ=0
    g11: LineSegment StartX=9.825 StartY=10 StartZ=0 EndX=9.825 EndY=0 EndZ=0
    g12: LineSegment StartX=9.825 StartY=0 StartZ=0 EndX=13 EndY=0 EndZ=0
    g13: LineSegment StartX=13 StartY=0 StartZ=0 EndX=13 EndY=10 EndZ=0
    g14: LineSegment StartX=-11.5 StartY=13.175 StartZ=0 EndX=9.825 EndY=13.175 EndZ=0
    g15: ArcOfCircle CenterX=9.825 CenterY=10 CenterZ=0 NormalX=0 NormalY=0 NormalZ=1 AngleXU=0 Radius=3.175 StartAngle=1e-16 EndAngle=1.5708
    g16: GeomPoint X=9.825 Y=-10 Z=0
  constraints (40):
    c: Horizontal(g2)
    c: PointOnObject(g3,g-1)
    c: Vertical(g3)
    c: Coincident(g4,g3)
    c: PointOnObject(g4,g-1)
    c: Coincident(g5,g4)
    c: Vertical(g5)
    c: Horizontal(g6)
    c: Tangent(g7,g5) = -1.5708
    c: Tangent(g7,g6) = 1.5708
    c: DistanceX(g4) = 13
    c: Tangent(g2,g1) = -1.5708
    c: Tangent(g6,g1) = 1.5708
    c: Diameter(g1) = 3.175
    c: DistanceX(g1) = -13
    c: Coincident(g7,g3)
    c: Coincident(g3,g2)
    c: Symmetric(g8,g2,g3)
    c: DistanceY(g8,g2) = 13  'cut_width'
    c: Horizontal(g10)
    c: PointOnObject(g11,g-1)
    c: Vertical(g11)
    c: Coincident(g12,g11)
    c: PointOnObject(g12,g-1)
    c: Coincident(g13,g12)
    c: Vertical(g13)
    c: Horizontal(g14)
    c: Tangent(g15,g13) = -1.5708
    c: Tangent(g15,g14) = 1.5708
    c: DistanceX(g12) = 13
    c: Tangent(g10,g9) = -1.5708
    c: Tangent(g14,g9) = 1.5708
    c: Diameter(g9) = 3.175
    c: DistanceX(g9) = -11.5
    c: Coincident(g15,g11)
    c: Coincident(g11,g10)
    c: Symmetric(g16,g10,g11)
    c: DistanceY(g16,g10) = 20  'cut_width'
    c: Coincident(g0,g1)
    c: Symmetric(g0,g0,g-1)
FEATURE [Sketcher::SketchObject] Sketch063
  AttachmentOffset = pos=(0,180.388,0) rot=(0,0,1;0rad)
  FullyConstrained = true
  MapMode = 5
  Placement = pos=(-156.22,-90.1938,0) rot=(0,0,1;2.0944rad)
  Support = -> [DatumPlane019]
  expr: .Constraints.cut_width = Sketch051.Constraints[18]
  expr: AttachmentOffset = Sketch051.AttachmentOffset
  expr: Constraints[10] = Sketch051.Constraints[10]
  expr: Constraints[13] = Sketch051.Constraints[13]
  expr: Constraints[14] = Sketch051.Constraints[14]
  sketch-geometry (9):
    g0: ArcOfCircle CenterX=-11.5 CenterY=8.0875 CenterZ=0 NormalX=0 NormalY=0 NormalZ=1 AngleXU=0 Radius=1.5875 StartAngle=1.5708 EndAngle=4.71239
    g1: LineSegment StartX=-11.5 StartY=6.5 StartZ=0 EndX=9.825 EndY=6.5 EndZ=0
    g2: LineSegment StartX=9.825 StartY=6.5 StartZ=0 EndX=9.825 EndY=0 EndZ=0
    g3: LineSegment StartX=9.825 StartY=0 StartZ=0 EndX=13 EndY=0 EndZ=0
    g4: LineSegment StartX=13 StartY=0 StartZ=0 EndX=13 EndY=6.5 EndZ=0
    g5: LineSegment StartX=-11.5 StartY=9.675 StartZ=0 EndX=9.825 EndY=9.675 EndZ=0
    g6: ArcOfCircle CenterX=9.825 CenterY=6.5 CenterZ=0 NormalX=0 NormalY=0 NormalZ=1 AngleXU=0 Radius=3.175 StartAngle=0 EndAngle=1.5708
    g7: GeomPoint X=9.825 Y=-6.5 Z=0
    g8: LineSegment StartX=11.5 StartY=8.0875 StartZ=0 EndX=11.5 EndY=-8.0875 EndZ=0
  constraints (22):
    c: Horizontal(g1)
    c: PointOnObject(g2,g-1)
    c: Vertical(g2)
    c: Coincident(g3,g2)
    c: PointOnObject(g3,g-1)
    c: Coincident(g4,g3)
    c: Vertical(g4)
    c: Horizontal(g5)
    c: Tangent(g6,g4) = -1.5708
    c: Tangent(g6,g5) = 1.5708
    c: DistanceX(g3) = 13
    c: Tangent(g1,g0) = -1.5708
    c: Tangent(g5,g0) = 1.5708
    c: Diameter(g0) = 3.175
    c: DistanceX(g0) = -11.5
    c: Coincident(g6,g2)
    c: Coincident(g2,g1)
    c: Symmetric(g7,g1,g2)
    c: DistanceY(g7,g1) = 13  'cut_width'
    c: Vertical(g8)
    c: Symmetric(g0,g8,g-1)
    c: Horizontal(g8,g0)
FEATURE [Sketcher::SketchObject] Sketch064
  AttachmentOffset = pos=(0,180.388,0) rot=(0,0,1;0rad)
  FullyConstrained = true
  MapMode = 5
  Placement = pos=(156.22,-90.1938,0) rot=(0,0,-1;2.0944rad)
  Support = -> [DatumPlane020]
  expr: .Constraints.cut_width = Sketch051.Constraints[18]
  expr: AttachmentOffset = Sketch051.AttachmentOffset
  expr: Constraints[10] = Sketch051.Constraints[10]
  expr: Constraints[13] = Sketch051.Constraints[13]
  expr: Constraints[14] = Sketch051.Constraints[14]
  sketch-geometry (9):
    g0: ArcOfCircle CenterX=-11.5 CenterY=8.0875 CenterZ=0 NormalX=0 NormalY=0 NormalZ=1 AngleXU=0 Radius=1.5875 StartAngle=1.5708 EndAngle=4.71239
    g1: LineSegment StartX=-11.5 StartY=6.5 StartZ=0 EndX=9.825 EndY=6.5 EndZ=0
    g2: LineSegment StartX=9.825 StartY=6.5 StartZ=0 EndX=9.825 EndY=0 EndZ=0
    g3: LineSegment StartX=9.825 StartY=0 StartZ=0 EndX=13 EndY=0 EndZ=0
    g4: LineSegment StartX=13 StartY=0 StartZ=0 EndX=13 EndY=6.5 EndZ=0
    g5: LineSegment StartX=-11.5 StartY=9.675 StartZ=0 EndX=9.825 EndY=9.675 EndZ=0
    g6: ArcOfCircle CenterX=9.825 CenterY=6.5 CenterZ=0 NormalX=0 NormalY=0 NormalZ=1 AngleXU=0 Radius=3.175 StartAngle=0 EndAngle=1.5708
    g7: GeomPoint X=9.825 Y=-6.5 Z=0
    g8: LineSegment StartX=11.5 StartY=8.0875 StartZ=0 EndX=11.5 EndY=-8.0875 EndZ=0
  constraints (22):
    c: Horizontal(g1)
    c: PointOnObject(g2,g-1)
    c: Vertical(g2)
    c: Coincident(g3,g2)
    c: PointOnObject(g3,g-1)
    c: Coincident(g4,g3)
    c: Vertical(g4)
    c: Horizontal(g5)
    c: Tangent(g6,g4) = -1.5708
    c: Tangent(g6,g5) = 1.5708
    c: DistanceX(g3) = 13
    c: Tangent(g1,g0) = -1.5708
    c: Tangent(g5,g0) = 1.5708
    c: Diameter(g0) = 3.175
    c: DistanceX(g0) = -11.5
    c: Coincident(g6,g2)
    c: Coincident(g2,g1)
    c: Symmetric(g7,g1,g2)
    c: DistanceY(g7,g1) = 13  'cut_width'
    c: Vertical(g8)
    c: Symmetric(g0,g8,g-1)
    c: Horizontal(g8,g0)
FEATURE [Sketcher::SketchObject] Sketch075
  AttachmentOffset = pos=(0,0,0) rot=(0,0,1;3.14159rad)
  FullyConstrained = true
  MapMode = 5
  Placement = pos=(0,0,0) rot=(0,0,1;3.14159rad)
  Support = -> [XY_Plane016]
  expr: Constraints[12] = 186.5mm - 3.175mm
  expr: Constraints[6] = <<main>>.rivet_d
  sketch-geometry (6):
    g0: Circle CenterX=64.8152 CenterY=64.8152 CenterZ=0 NormalX=0 NormalY=0 NormalZ=1 AngleXU=0 Radius=1.7
    g1: Circle CenterX=64.8152 CenterY=-64.8152 CenterZ=0 NormalX=0 NormalY=0 NormalZ=1 AngleXU=0 Radius=1.7
    g2: Circle CenterX=-64.8152 CenterY=-64.8152 CenterZ=0 NormalX=0 NormalY=0 NormalZ=1 AngleXU=0 Radius=1.7
    g3: Circle CenterX=-64.8152 CenterY=64.8152 CenterZ=0 NormalX=0 NormalY=0 NormalZ=1 AngleXU=0 Radius=1.7
    g4: LineSegment StartX=-64.8152 StartY=64.8152 StartZ=0 EndX=64.8152 EndY=64.8152 EndZ=0
    g5: LineSegment StartX=64.8152 StartY=64.8152 StartZ=0 EndX=64.8152 EndY=-64.8152 EndZ=0
  constraints (13):
    c: Symmetric(g3,g0,g-2)
    c: Symmetric(g0,g1,g-1)
    c: Symmetric(g0,g2,g-1)
    c: Equal(g0,g3)
    c: Equal(g0,g2)
    c: Equal(g0,g1)
    c: Diameter(g0) = 3.4
    c: Coincident(g4,g3)
    c: Coincident(g4,g0)
    c: Coincident(g5,g0)
    c: Coincident(g5,g1)
    c: Equal(g5,g4)
    c: Distance(g2,g0) = 183.325
FEATURE [PartDesign::Pocket] Pocket036
  BaseFeature = -> Pocket027
  Direction = (0,0,-1)
  Length = 5
  Length2 = 5
  Midplane = true
  Profile = -> Sketch075
  ReferenceAxis = -> Sketch075 [N_Axis]
  Type = 1
FEATURE [PartDesign::SubShapeBinder] Binder018
  BindCopyOnChange = 0
  BindMode = 0
  ClaimChildren = true
  Context = -> Body001003005003 [Binder018.]
  Fuse = false
  MakeFace = true
  OffsetFill = false
  OffsetIntersection = false
  OffsetJoinType = 0
  OffsetOpenResult = false
  PartialLoad = false
  Relative = false
  Support = -> [Body001003005003012[Pocket039.Sketch080.]]
  _Version = 2
FEATURE [PartDesign::SubShapeBinder] Binder023
  BindCopyOnChange = 0
  BindMode = 0
  ClaimChildren = false
  Context = -> Body001003005003 [Binder023.]
  Fuse = false
  MakeFace = true
  OffsetFill = false
  OffsetIntersection = false
  OffsetJoinType = 0
  OffsetOpenResult = false
  PartialLoad = false
  Relative = true
  Support = -> [Body001003005003013[Pocket042.Sketch084.,Pocket041.Sketch083.]]
  _Version = 2
FEATURE [PartDesign::SubShapeBinder] Binder036
  BindCopyOnChange = 0
  BindMode = 0
  ClaimChildren = false
  Context = -> Body001003005003 [Binder036.]
  Fuse = false
  MakeFace = true
  OffsetFill = false
  OffsetIntersection = false
  OffsetJoinType = 0
  OffsetOpenResult = false
  PartialLoad = false
  Placement = pos=(13,180,0) rot=(0,0,1;1.5708rad)
  Relative = true
  Support = -> [Body_7[Pocket061.Sketch105.]]
  _Version = 2
  expr: .Placement.Base.x = <<main>>.end_face_width / 2 - <<main>>.thickness
  expr: .Placement.Base.y = Sketch119.AttachmentOffset.Base.x
FEATURE [PartDesign::Pocket] Pocket074
  BaseFeature = -> Pocket036
  Direction = (0,0,-1)
  Length = 5
  Length2 = 5
  Midplane = true
  Profile = -> Binder036
  Type = 1
FEATURE [PartDesign::Mirrored] Mirrored
  MirrorPlane = -> YZ_Plane015
FEATURE [PartDesign::PolarPattern] PolarPattern015
  Angle = 360
  Axis = -> Z_Axis015
  Occurrences = 3
FEATURE [PartDesign::MultiTransform] MultiTransform
  BaseFeature = -> Pocket074
  Originals = -> [Pocket074]
  Transformations = -> [Mirrored,PolarPattern015]
FEATURE [Sketcher::SketchObject] Sketch120
  AttachmentOffset = pos=(0,-70,0) rot=(0,0,1;0rad)
  FullyConstrained = true
  MapMode = 5
  Placement = pos=(0,-70,0) rot=(0,0,1;0rad)
  Support = -> [XY_Plane016]
  sketch-geometry (1):
    g0: Circle CenterX=0 CenterY=0 CenterZ=0 NormalX=0 NormalY=0 NormalZ=1 AngleXU=0 Radius=4.25
  constraints (2):
    c: Coincident(g0,g-1)
    c: Diameter(g0) = 8.5
FEATURE [PartDesign::Pocket] Pocket087
  BaseFeature = -> MultiTransform
  Direction = (0,0,-1)
  Length = 5
  Length2 = 5
  Midplane = true
  Profile = -> Binder023
  Type = 1
FEATURE [PartDesign::PolarPattern] PolarPattern018
  Angle = 120
  Axis = -> Z_Axis015
  BaseFeature = -> Pocket087
  Occurrences = 2
  Originals = -> [Pocket087]
FEATURE [Sketcher::SketchObject] Sketch132
  FullyConstrained = true
  MapMode = 5
  Support = -> [XY_Plane016]
  expr: Constraints[1] = Sketch048.Constraints[1]
  sketch-geometry (3):
    g0: Circle CenterX=0 CenterY=0 CenterZ=0 NormalX=0 NormalY=0 NormalZ=1 AngleXU=0 Radius=212.348
    g1: Circle CenterX=0 CenterY=0 CenterZ=0 NormalX=0 NormalY=0 NormalZ=1 AngleXU=0 Radius=202.348
    g2: LineSegment StartX=202.348 StartY=0 StartZ=0 EndX=212.348 EndY=0 EndZ=0
  constraints (8):
    c: Coincident(g0,g-1)
    c: Radius(g0) = 212.348
    c: Coincident(g1,g0)
    c: PointOnObject(g2,g1)
    c: PointOnObject(g2,g0)
    c: Horizontal(g2)
    c: PointOnObject(g0,g2)
    c: DistanceX(g2,g2) = 10
FEATURE [PartDesign::Pad] Pad030
  BaseFeature = -> PolarPattern018
  Direction = (0,0,1)
  Length = 3
  Length2 = 10
  Profile = -> Sketch132
  ReferenceAxis = -> Sketch132 [N_Axis]
  Type = 0
  expr: Length = Pad013.Length
FEATURE [PartDesign::Body] Body001003005003  label="basement"
  Group = -> [Sketch048,Pad013,Sketch049,Binder004,DatumPlane017,Sketch050,Local_CS017,Sketch051,Binder005,DatumPlane018,Sketch057,Sketch058,Pocket027,Local_CS021,Local_CS022,DatumPlane019,DatumPlane020,Sketch061,Sketch062,Sketch063,Sketch064,Sketch075,Pocket036,Binder018,Binder023,Binder036,Pocket074,MultiTransform,Mirrored,PolarPattern015,Sketch120,Pocket087,PolarPattern018,Sketch132,Pad030]
  Origin = -> Origin015
  Tip = -> Pad030
COMPONENT P5 — recipe-attached ("Body001003005003003", modeled in this document).
Construction recipe (the document's own serialized feature program — sketch geometry with constraints, then the solid features built on it; lengths are millimeters unless a unit is written):

FEATURE [Sketcher::SketchObject] Sketch052
  FullyConstrained = true
  MapMode = 5
  Support = -> [XY_Plane017]
  expr: .Constraints.r = Sketch003.Constraints.max_r
  expr: Constraints[13] = 15mm + <<main>>.end_face_width / 2
  sketch-geometry (6):
    g0: ArcOfCircle CenterX=0 CenterY=0 CenterZ=0 NormalX=0 NormalY=0 NormalZ=1 AngleXU=0 Radius=199.848 StartAngle=0.699923 EndAngle=1.5708
    g1: ArcOfCircle CenterX=0 CenterY=0 CenterZ=0 NormalX=0 NormalY=0 NormalZ=1 AngleXU=0 Radius=209.848 StartAngle=0.699923 EndAngle=1.5708
    g2: ArcOfCircle CenterX=156.687 CenterY=131.955 CenterZ=0 NormalX=0 NormalY=0 NormalZ=1 AngleXU=0 Radius=5 StartAngle=3.84152 EndAngle=6.98311
    g3: LineSegment StartX=1.22e-14 StartY=199.848 StartZ=0 EndX=1.28e-14 EndY=209.848 EndZ=0
    g4: ArcOfCircle CenterX=0 CenterY=0 CenterZ=0 NormalX=0 NormalY=0 NormalZ=1 AngleXU=0 Radius=204.848 StartAngle=0.675514 EndAngle=1.5708
    g5: LineSegment StartX=0 StartY=0 StartZ=0 EndX=177.404 EndY=102.424 EndZ=0
  constraints (18):
    c: Coincident(g0,g-1)
    c: PointOnObject(g0,g-2)
    c: Coincident(g1,g0)
    c: PointOnObject(g1,g-2)
    c: Coincident(g3,g1)
    c: DistanceY(g1) = 209.848  'r'
    c: DistanceY(g0,g1) = 10  'width'
    c: Tangent(g2,g0) = 1.5708
    c: Tangent(g2,g1) = -1.5708
    c: Coincident(g4,g0)
    c: PointOnObject(g4,g2)
    c: Coincident(g5,g0)
    c: Angle(g-1,g5) = 0.523599
    c: Distance(g4,g5) = 31
    c: Coincident(g3,g0)
    c: PointOnObject(g2,g4)
    c: PointOnObject(g4,g-2)
    c: PointOnObject(g5,g4)
FEATURE [PartDesign::Pad] Pad014
  Direction = (0,0,1)
  Length = 3
  Length2 = 10
  Profile = -> Sketch052
  ReferenceAxis = -> Sketch052 [N_Axis]
  Type = 0
FEATURE [PartDesign::CoordinateSystem] Local_CS018
  AttacherType = Attacher::AttachEngine3D
  MapMode = 5
  Support = -> [XY_Plane017]
FEATURE [Sketcher::SketchObject] Sketch055
  FullyConstrained = true
  MapMode = 5
  Support = -> [XY_Plane017]
  expr: .Constraints.r = Sketch052.Constraints[5]
  expr: .Constraints.width = Sketch052.Constraints[6]
  expr: Constraints[12] = Sketch052.Constraints[12]
  expr: Constraints[13] = Sketch052.Constraints[13]
  expr: Constraints[25] = <<main>>.rivet_d
  sketch-geometry (9):
    g0: ArcOfCircle CenterX=0 CenterY=0 CenterZ=0 NormalX=0 NormalY=0 NormalZ=1 AngleXU=0 Radius=199.848 StartAngle=0.699923 EndAngle=1.5708
    g1: ArcOfCircle CenterX=0 CenterY=0 CenterZ=0 NormalX=0 NormalY=0 NormalZ=1 AngleXU=0 Radius=209.848 StartAngle=0.699923 EndAngle=1.5708
    g2: ArcOfCircle CenterX=156.687 CenterY=131.955 CenterZ=0 NormalX=0 NormalY=0 NormalZ=1 AngleXU=0 Radius=5 StartAngle=3.84152 EndAngle=6.98311
    g3: LineSegment StartX=1.22e-14 StartY=199.848 StartZ=0 EndX=1.28e-14 EndY=209.848 EndZ=0
    g4: ArcOfCircle CenterX=0 CenterY=0 CenterZ=0 NormalX=0 NormalY=0 NormalZ=1 AngleXU=0 Radius=204.848 StartAngle=0.675514 EndAngle=1.5708
    g5: LineSegment StartX=0 StartY=0 StartZ=0 EndX=177.404 EndY=102.424 EndZ=0
    g6: LineSegment StartX=1.22e-14 StartY=203.148 StartZ=0 EndX=1.31e-14 EndY=206.548 EndZ=0
    g7: ArcOfCircle CenterX=1.25e-14 CenterY=204.848 CenterZ=0 NormalX=0 NormalY=0 NormalZ=1 AngleXU=0 Radius=1.7 StartAngle=4.71239 EndAngle=7.85398
    g8: Circle CenterX=143.11 CenterY=146.569 CenterZ=0 NormalX=0 NormalY=0 NormalZ=1 AngleXU=0 Radius=1.7
  constraints (27):
    c: Coincident(g0,g-1)
    c: PointOnObject(g0,g-2)
    c: Coincident(g1,g0)
    c: PointOnObject(g1,g-2)
    c: Coincident(g3,g1)
    c: DistanceY(g1) = 209.848  'r'
    c: DistanceY(g0,g1) = 10  'width'
    c: Tangent(g2,g0) = 1.5708
    c: Tangent(g2,g1) = -1.5708
    c: Coincident(g4,g0)
    c: PointOnObject(g4,g2)
    c: Coincident(g5,g0)
    c: Angle(g-1,g5) = 0.523599
    c: Distance(g4,g5) = 31
    c: Coincident(g3,g0)
    c: PointOnObject(g2,g4)
    c: PointOnObject(g4,g-2)
    c: PointOnObject(g5,g4)
    c: PointOnObject(g6,g3)
    c: PointOnObject(g6,g3)
    c: Coincident(g7,g4)
    c: Coincident(g7,g6)
    c: Coincident(g7,g6)
    c: PointOnObject(g8,g4)
    c: Equal(g8,g7)
    c: Diameter(g7) = 3.4
    c: DistanceX(g8) = 143.11
FEATURE [PartDesign::Pocket] Pocket019
  BaseFeature = -> Pad014
  Direction = (0,0,-1)
  Length = 5
  Length2 = 5
  Midplane = true
  Profile = -> Sketch055
  ReferenceAxis = -> Sketch055 [N_Axis]
  Type = 1
FEATURE [PartDesign::Mirrored] Mirrored019
  BaseFeature = -> Pocket019
  MirrorPlane = -> Sketch052 [V_Axis]
  Originals = -> [Pad014,Pocket019]
FEATURE [PartDesign::Body] Body001003005003003
  Group = -> [Sketch052,Pad014,Pocket019,Mirrored019,Local_CS018,Sketch055]
  Origin = -> Origin016
  Tip = -> Mirrored019
COMPONENT P6 — recipe-attached ("basement2", modeled in this document).
Construction recipe (the document's own serialized feature program — sketch geometry with constraints, then the solid features built on it; lengths are millimeters unless a unit is written):

FEATURE [Sketcher::SketchObject] Sketch076
  FullyConstrained = true
  MapMode = 5
  Support = -> [XY_Plane025]
  expr: Constraints[1] = (180mm - 11.5mm) * 2
  sketch-geometry (1):
    g0: Circle CenterX=0 CenterY=0 CenterZ=0 NormalX=0 NormalY=0 NormalZ=1 AngleXU=0 Radius=168.5
  constraints (2):
    c: Coincident(g0,g-1)
    c: Diameter(g0) = 337
FEATURE [PartDesign::Pad] Pad020
  Direction = (0,0,1)
  Length = 3
  Length2 = 10
  Profile = -> Sketch076
  ReferenceAxis = -> Sketch076 [N_Axis]
  Type = 0
FEATURE [PartDesign::SubShapeBinder] Binder044
  BindCopyOnChange = 0
  BindMode = 0
  ClaimChildren = false
  Context = -> Body001003005003011 [Binder044.]
  Fuse = false
  MakeFace = true
  OffsetFill = false
  OffsetIntersection = false
  OffsetJoinType = 0
  OffsetOpenResult = false
  PartialLoad = false
  Relative = true
  Support = -> [Body001003005003[Pocket036.Sketch075.]]
  _Version = 2
FEATURE [PartDesign::SubShapeBinder] Binder045
  BindCopyOnChange = 0
  BindMode = 0
  ClaimChildren = false
  Context = -> Body001003005003011 [Binder045.]
  Fuse = false
  MakeFace = true
  OffsetFill = false
  OffsetIntersection = false
  OffsetJoinType = 0
  OffsetOpenResult = false
  PartialLoad = false
  Placement = pos=(0,0,0) rot=(0,0,1;0.785398rad)
  Relative = true
  Support = -> [Body001003005003[Pocket036.Sketch075.]]
  _Version = 2
FEATURE [PartDesign::Pocket] Pocket088
  BaseFeature = -> Pad020
  Direction = (0,0,-1)
  Length = 5
  Length2 = 5
  Midplane = true
  Profile = -> Binder044
  Type = 1
FEATURE [PartDesign::Hole] Hole
  BaseFeature = -> Pocket088
  CustomThreadClearance = 0
  Depth = 25
  DepthType = 0
  Diameter = 15.5
  DrillForDepth = false
  DrillPoint = 1
  DrillPointAngle = 118
  HoleCutCountersinkAngle = 90
  HoleCutCustomValues = false
  HoleCutDepth = 0
  HoleCutDiameter = 6.1
  HoleCutType = 0
  ModelThread = false
  Profile = -> Binder045
  Reversed = true
  Tapered = false
  TaperedAngle = 90
  ThreadClass = 0
  ThreadDepth = 25
  ThreadDepthType = 0
  ThreadDirection = 0
  ThreadFit = 0
  ThreadSize = 0
  ThreadType = 0
  Threaded = false
  UseCustomThreadClearance = false
FEATURE [PartDesign::Body] Body001003005003011  label="basement2"
  Group = -> [Sketch076,Pad020,Binder044,Binder045,Pocket088,Hole]
  Origin = -> Origin024
  Tip = -> Hole
COMPONENT P7 — recipe-attached ("Body001003005003012", modeled in this document).
Construction recipe (the document's own serialized feature program — sketch geometry with constraints, then the solid features built on it; lengths are millimeters unless a unit is written):

FEATURE [Sketcher::SketchObject] Sketch078
  FullyConstrained = true
  MapMode = 5
  Placement = pos=(0,0,0) rot=(1,0,0;1.5708rad)
  Support = -> [XZ_Plane025]
FEATURE [Sketcher::SketchObject] Sketch079
  FullyConstrained = true
  MapMode = 5
  Placement = pos=(0,0,0) rot=(0.57735,0.57735,0.57735;2.0944rad)
  Support = -> [YZ_Plane025]
  expr: Constraints[8] = <<main>>.basin_height
  sketch-geometry (3):
    g0: LineSegment StartX=15 StartY=0 StartZ=0 EndX=0 EndY=0 EndZ=0
    g1: LineSegment StartX=0 StartY=0 StartZ=0 EndX=0 EndY=157 EndZ=0
    g2: LineSegment StartX=0 StartY=157 StartZ=0 EndX=15 EndY=157 EndZ=0
  constraints (9):
    c: PointOnObject(g0,g-1)
    c: Coincident(g0,g-1)
    c: Coincident(g1,g0)
    c: PointOnObject(g1,g-2)
    c: Coincident(g2,g1)
    c: Horizontal(g2)
    c: DistanceX(g0,g0) = 15
    c: Vertical(g0,g2)
    c: DistanceY(g1) = 157
FEATURE [PartDesign::FeaturePython] BaseBend  # WARN: FeaturePython — macro-defined, semantics opaque (R4)
  BendSide = 0
  BendSketch = -> Sketch079
  MidPlane = true
  Reverse = false
  length = 15
  radius = 2
  thickness = 1
FEATURE [Sketcher::SketchObject] Sketch080
  AttachmentOffset = pos=(0,7.5,0) rot=(0,0,1;0rad)
  FullyConstrained = true
  MapMode = 5
  Placement = pos=(0,7.5,0) rot=(0,0,1;0rad)
  Support = -> [XY_Plane026]
  sketch-geometry (1):
    g0: Circle CenterX=0 CenterY=0 CenterZ=0 NormalX=0 NormalY=0 NormalZ=1 AngleXU=0 Radius=1.65
  constraints (3):
    c: PointOnObject(g0,g-2)
    c: Diameter(g0) = 3.3
    c: DistanceY(g0) = 0
FEATURE [PartDesign::Pocket] Pocket039
  BaseFeature = -> BaseBend
  Direction = (0,0,-1)
  Length = 5
  Length2 = 5
  Profile = -> Sketch080
  ReferenceAxis = -> Sketch080 [N_Axis]
  Reversed = true
  Type = 1
FEATURE [Sketcher::SketchObject] Sketch081
  FullyConstrained = true
  MapMode = 5
  Support = -> [XY_Plane026]
  sketch-geometry (3):
    g0: ArcOfCircle CenterX=4.5 CenterY=12 CenterZ=0 NormalX=0 NormalY=0 NormalZ=1 AngleXU=0 Radius=3 StartAngle=1e-16 EndAngle=1.57079
    g1: LineSegment StartX=4.50001 StartY=15 StartZ=0 EndX=7.5 EndY=15 EndZ=0
    g2: LineSegment StartX=7.5 StartY=12 StartZ=0 EndX=7.5 EndY=15 EndZ=0
  constraints (9):
    c: Diameter(g0) = 6
    c: Coincident(g1,g0)
    c: Tangent(g1,g0)
    c: Coincident(g2,g1)
    c: Vertical(g2)
    c: Horizontal(g1)
    c: DistanceX(g1) = 7.5
    c: DistanceY(g1) = 15
    c: Tangent(g2,g0) = -1.5708
FEATURE [PartDesign::Pocket] Pocket040
  BaseFeature = -> Pocket039
  Direction = (0,0,-1)
  Length = 5
  Length2 = 5
  Midplane = true
  Profile = -> Sketch081
  ReferenceAxis = -> Sketch081 [N_Axis]
  Type = 1
FEATURE [PartDesign::Mirrored] Mirrored028
  BaseFeature = -> Pocket040
  MirrorPlane = -> Sketch081 [V_Axis]
  Originals = -> [Pocket040]
FEATURE [PartDesign::Body] Body001003005003012
  Group = -> [Sketch078,Sketch079,BaseBend,Sketch080,Pocket039,Sketch081,Pocket040,Mirrored028]
  Origin = -> Origin025
  Tip = -> Mirrored028
COMPONENT P8 — recipe-attached ("plexiglass_holder_top", modeled in this document).
Construction recipe (the document's own serialized feature program — sketch geometry with constraints, then the solid features built on it; lengths are millimeters unless a unit is written):

FEATURE [Sketcher::SketchObject] Sketch082
  FullyConstrained = false
  MapMode = 5
  Support = -> [XY_Plane027]
  expr: Constraints[20] = <<main>>.end_face_width / 2 + 2mm
  expr: Constraints[2] = Sketch052.Constraints.r - Sketch052.Constraints.width - 2mm
  expr: Constraints[41] = <<main>>.end_face_width / 2
  sketch-geometry (19):
    g0: ArcOfCircle CenterX=0 CenterY=1.42e-14 CenterZ=0 NormalX=0 NormalY=0 NormalZ=1 AngleXU=0 Radius=197.848 StartAngle=0.657286 EndAngle=1.5708
    g1: LineSegment StartX=1.21e-14 StartY=197.848 StartZ=0 EndX=1.12e-14 EndY=182.848 EndZ=0
    g2: ArcOfCircle CenterX=0 CenterY=1.42e-14 CenterZ=0 NormalX=0 NormalY=0 NormalZ=1 AngleXU=0 Radius=182.848 StartAngle=0.657286 EndAngle=1.5708
    g3: ArcOfCircle CenterX=150.69 CenterY=116.297 CenterZ=0 NormalX=0 NormalY=0 NormalZ=1 AngleXU=0 Radius=7.5 StartAngle=3.79888 EndAngle=6.94047
    g4: LineSegment StartX=0 StartY=1.42e-14 StartZ=0 EndX=165.582 EndY=95.5988 EndZ=0
    g5: GeomPoint X=155.154 Y=110.271 Z=0
    g6: LineSegment StartX=165.582 StartY=95.5988 StartZ=0 EndX=155.154 EndY=110.271 EndZ=0
    g7: ArcOfCircle CenterX=0 CenterY=1.42e-14 CenterZ=0 NormalX=0 NormalY=0 NormalZ=1 AngleXU=0 Radius=190.348 StartAngle=0.617882 EndAngle=1.5708
    g8: ArcOfCircle CenterX=0 CenterY=1.42e-14 CenterZ=0 NormalX=0 NormalY=0 NormalZ=1 AngleXU=0 Radius=190.348 StartAngle=0.641212 EndAngle=1.5708
    g9: ArcOfCircle CenterX=0 CenterY=1.42e-14 CenterZ=0 NormalX=0 NormalY=0 NormalZ=1 AngleXU=0 Radius=197.848 StartAngle=0.619862 EndAngle=0.657286
    g10: LineSegment StartX=155.154 StartY=110.271 StartZ=0 EndX=160.726 EndY=113.488 EndZ=0
    g11: ArcOfCircle CenterX=160.226 CenterY=114.354 CenterZ=0 NormalX=0 NormalY=0 NormalZ=1 AngleXU=0 Radius=1 StartAngle=5.23599 EndAngle=6.90305
    g12: ArcOfCircle CenterX=0 CenterY=1.42e-14 CenterZ=0 NormalX=0 NormalY=0 NormalZ=1 AngleXU=0 Radius=182.848 StartAngle=0.626692 EndAngle=0.657286
    g13: LineSegment StartX=155.154 StartY=110.271 StartZ=0 EndX=149.412 EndY=106.955 EndZ=0
    g14: ArcOfCircle CenterX=148.912 CenterY=107.821 CenterZ=0 NormalX=0 NormalY=0 NormalZ=1 AngleXU=0 Radius=1 StartAngle=3.76829 EndAngle=5.23599
    g15: ArcOfCircle CenterX=0 CenterY=1.42e-14 CenterZ=0 NormalX=0 NormalY=0 NormalZ=1 AngleXU=0 Radius=197.848 StartAngle=0.604557 EndAngle=1.5708
    g16: LineSegment StartX=162.781 StartY=112.457 StartZ=0 EndX=0 EndY=1.42e-14 EndZ=0
    g17: LineSegment StartX=162.781 StartY=112.457 StartZ=0 EndX=0 EndY=112.457 EndZ=0
    g18: LineSegment StartX=0 StartY=1.42e-14 StartZ=0 EndX=162.781 EndY=112.457 EndZ=0
  constraints (52):
    c: Coincident(g0,g-1)
    c: PointOnObject(g0,g-2)
    c: DistanceY(g0) = 197.848
    c: Coincident(g1,g0)
    c: PointOnObject(g1,g-2)
    c: Coincident(g2,g0)
    c: Coincident(g2,g1)
    c: Tangent(g3,g0) = -1.5708
    c: Tangent(g3,g2) = 1.5708
    c: DistanceY(g1,g1) = 15
    c: Coincident(g4,g0)
    c: Angle(g-1,g4) = 0.523599
    c: PointOnObject(g5,g3)
    c: Coincident(g6,g4)
    c: Coincident(g6,g5)
    c: Coincident(g7,g0)
    c: Coincident(g7,g5)
    c: PointOnObject(g7,g1)
    c: PointOnObject(g3,g7)
    c: Tangent(g6,g7)
    c: Distance(g6) = 18
    c: Coincident(g8,g0)
    c: PointOnObject(g8,g-2)
    c: DistanceY(g8,g0) = 7.5
    c: Coincident(g9,g0)
    c: Coincident(g9,g0)
    c: Coincident(g10,g5)
    c: Parallel(g10,g4)
    c: Tangent(g9,g11) = -1.5708
    c: Tangent(g10,g11) = -1.5708
    c: Diameter(g11) = 2
    c: Coincident(g12,g0)
    c: Coincident(g12,g2)
    c: Coincident(g13,g10)
    c: Parallel(g13,g10)
    c: Tangent(g12,g14) = 1.5708
    c: Tangent(g13,g14) = 1.5708
    c: Equal(g14,g11)
    c: Coincident(g15,g0)
    c: PointOnObject(g15,g-2)
    c: Equal(g15,g9)
    c: Distance(g15,g4) = 16
    c: Coincident(g16,g15)
    c: Coincident(g16,g0)
    c: Angle(g16,g-2) = 0.966239
    c: Coincident(g17,g15)
    c: PointOnObject(g17,g-2)
    c: Horizontal(g17)
    c: DistanceX(g17,g17) = 162.781
    c: Coincident(g18,g0)
    c: Coincident(g18,g15)
    c: Angle(g16,g-2) = 0.966239
FEATURE [PartDesign::Pad] Pad021
  Direction = (0,0,1)
  Length = 3
  Length2 = 10
  Profile = -> Sketch082
  ReferenceAxis = -> Sketch082 [N_Axis]
  Type = 0
FEATURE [Sketcher::SketchObject] Sketch083
  FullyConstrained = true
  MapMode = 5
  Support = -> [XY_Plane027]
  expr: Constraints[11] = Sketch082.Constraints[11]
  expr: Constraints[20] = Sketch082.Constraints[20]
  expr: Constraints[23] = Sketch082.Constraints[23]
  expr: Constraints[25] = <<main>>.rivet_d
  expr: Constraints[2] = Sketch082.Constraints[2]
  expr: Constraints[9] = Sketch082.Constraints[9]
  sketch-geometry (11):
    g0: ArcOfCircle CenterX=0 CenterY=0 CenterZ=0 NormalX=0 NormalY=0 NormalZ=1 AngleXU=0 Radius=197.848 StartAngle=0.657286 EndAngle=1.5708
    g1: LineSegment StartX=1.21e-14 StartY=197.848 StartZ=0 EndX=1.12e-14 EndY=182.848 EndZ=0
    g2: ArcOfCircle CenterX=0 CenterY=0 CenterZ=0 NormalX=0 NormalY=0 NormalZ=1 AngleXU=0 Radius=182.848 StartAngle=0.657286 EndAngle=1.5708
    g3: ArcOfCircle CenterX=150.69 CenterY=116.297 CenterZ=0 NormalX=0 NormalY=0 NormalZ=1 AngleXU=0 Radius=7.5 StartAngle=3.79888 EndAngle=6.94047
    g4: LineSegment StartX=0 StartY=0 StartZ=0 EndX=165.582 EndY=95.5988 EndZ=0
    g5: GeomPoint X=155.154 Y=110.271 Z=0
    g6: LineSegment StartX=165.582 StartY=95.5988 StartZ=0 EndX=155.154 EndY=110.271 EndZ=0
    g7: ArcOfCircle CenterX=0 CenterY=0 CenterZ=0 NormalX=0 NormalY=0 NormalZ=1 AngleXU=0 Radius=190.348 StartAngle=0.617882 EndAngle=1.5708
    g8: ArcOfCircle CenterX=0 CenterY=0 CenterZ=0 NormalX=0 NormalY=0 NormalZ=1 AngleXU=0 Radius=190.348 StartAngle=0.670423 EndAngle=1.5708
    g9: Circle CenterX=149.149 CenterY=118.267 CenterZ=0 NormalX=0 NormalY=0 NormalZ=1 AngleXU=0 Radius=1.7
    g10: Circle CenterX=-149.149 CenterY=118.267 CenterZ=0 NormalX=0 NormalY=0 NormalZ=1 AngleXU=0 Radius=1.7
  constraints (29):
    c: Coincident(g0,g-1)
    c: PointOnObject(g0,g-2)
    c: DistanceY(g0) = 197.848
    c: Coincident(g1,g0)
    c: PointOnObject(g1,g-2)
    c: Coincident(g2,g0)
    c: Coincident(g2,g1)
    c: Tangent(g3,g0) = -1.5708
    c: Tangent(g3,g2) = 1.5708
    c: DistanceY(g1,g1) = 15
    c: Coincident(g4,g0)
    c: Angle(g-1,g4) = 0.523599
    c: PointOnObject(g5,g3)
    c: Coincident(g6,g4)
    c: Coincident(g6,g5)
    c: Coincident(g7,g0)
    c: Coincident(g7,g5)
    c: PointOnObject(g7,g1)
    c: PointOnObject(g3,g7)
    c: Tangent(g6,g7)
    c: Distance(g6) = 18
    c: Coincident(g8,g0)
    c: PointOnObject(g8,g-2)
    c: DistanceY(g8,g0) = 7.5
    c: Coincident(g9,g8)
    c: Diameter(g9) = 3.4
    c: Symmetric(g10,g9,g-2)
    c: Equal(g10,g9)
    c: Distance(g5,g9) = 10
FEATURE [PartDesign::Mirrored] Mirrored029
  BaseFeature = -> Pad021
  MirrorPlane = -> Sketch082 [V_Axis]
  Originals = -> [Pad021]
  Refine = true
FEATURE [PartDesign::Pocket] Pocket041
  BaseFeature = -> Mirrored029
  Direction = (0,0,-1)
  Length = 5
  Length2 = 5
  Midplane = true
  Profile = -> Sketch083
  ReferenceAxis = -> Sketch083 [N_Axis]
  Type = 1
FEATURE [Sketcher::SketchObject] Sketch084
  FullyConstrained = true
  MapMode = 5
  Support = -> [XY_Plane027]
  expr: Constraints[11] = Sketch082.Constraints[11]
  expr: Constraints[20] = Sketch082.Constraints[20]
  expr: Constraints[27] = Sketch082.Constraints[30]
  expr: Constraints[2] = Sketch082.Constraints[2]
  expr: Constraints[36] = <<main>>.rivet_d
  expr: Constraints[9] = Sketch082.Constraints[9]
  sketch-geometry (15):
    g0: ArcOfCircle CenterX=0 CenterY=0 CenterZ=0 NormalX=0 NormalY=0 NormalZ=1 AngleXU=0 Radius=197.848 StartAngle=0.657286 EndAngle=1.5708
    g1: LineSegment StartX=1.21e-14 StartY=197.848 StartZ=0 EndX=1.12e-14 EndY=182.848 EndZ=0
    g2: ArcOfCircle CenterX=0 CenterY=0 CenterZ=0 NormalX=0 NormalY=0 NormalZ=1 AngleXU=0 Radius=182.848 StartAngle=0.657286 EndAngle=1.5708
    g3: ArcOfCircle CenterX=150.69 CenterY=116.297 CenterZ=0 NormalX=0 NormalY=0 NormalZ=1 AngleXU=0 Radius=7.5 StartAngle=3.79888 EndAngle=6.94047
    g4: LineSegment StartX=0 StartY=0 StartZ=0 EndX=165.582 EndY=95.5988 EndZ=0
    g5: GeomPoint X=155.154 Y=110.271 Z=0
    g6: LineSegment StartX=165.582 StartY=95.5988 StartZ=0 EndX=155.154 EndY=110.271 EndZ=0
    g7: ArcOfCircle CenterX=0 CenterY=0 CenterZ=0 NormalX=0 NormalY=0 NormalZ=1 AngleXU=0 Radius=190.348 StartAngle=0.617882 EndAngle=1.5708
    g8: ArcOfCircle CenterX=0 CenterY=0 CenterZ=0 NormalX=0 NormalY=0 NormalZ=1 AngleXU=0 Radius=197.848 StartAngle=0.619862 EndAngle=0.657286
    g9: LineSegment StartX=155.154 StartY=110.271 StartZ=0 EndX=160.726 EndY=113.488 EndZ=0
    g10: ArcOfCircle CenterX=160.226 CenterY=114.354 CenterZ=0 NormalX=0 NormalY=0 NormalZ=1 AngleXU=0 Radius=1 StartAngle=5.23599 EndAngle=6.90305
    g11: ArcOfCircle CenterX=0 CenterY=0 CenterZ=0 NormalX=0 NormalY=0 NormalZ=1 AngleXU=0 Radius=182.848 StartAngle=0.626692 EndAngle=0.657286
    g12: LineSegment StartX=155.154 StartY=110.271 StartZ=0 EndX=149.412 EndY=106.955 EndZ=0
    g13: ArcOfCircle CenterX=148.912 CenterY=107.821 CenterZ=0 NormalX=0 NormalY=0 NormalZ=1 AngleXU=0 Radius=1 StartAngle=3.76829 EndAngle=5.23599
    g14: Circle CenterX=1.17e-14 CenterY=190.348 CenterZ=0 NormalX=0 NormalY=0 NormalZ=1 AngleXU=0 Radius=1.7
  constraints (37):
    c: Coincident(g0,g-1)
    c: PointOnObject(g0,g-2)
    c: DistanceY(g0) = 197.848
    c: Coincident(g1,g0)
    c: PointOnObject(g1,g-2)
    c: Coincident(g2,g0)
    c: Coincident(g2,g1)
    c: Tangent(g3,g0) = -1.5708
    c: Tangent(g3,g2) = 1.5708
    c: DistanceY(g1,g1) = 15
    c: Coincident(g4,g0)
    c: Angle(g-1,g4) = 0.523599
    c: PointOnObject(g5,g3)
    c: Coincident(g6,g4)
    c: Coincident(g6,g5)
    c: Coincident(g7,g0)
    c: Coincident(g7,g5)
    c: PointOnObject(g7,g1)
    c: PointOnObject(g3,g7)
    c: Tangent(g6,g7)
    c: Distance(g6) = 18
    c: Coincident(g8,g0)
    c: Coincident(g8,g0)
    c: Coincident(g9,g5)
    c: Parallel(g9,g4)
    c: Tangent(g8,g10) = -1.5708
    c: Tangent(g9,g10) = -1.5708
    c: Diameter(g10) = 2
    c: Coincident(g11,g0)
    c: Coincident(g11,g2)
    c: Coincident(g12,g9)
    c: Parallel(g12,g9)
    c: Tangent(g11,g13) = 1.5708
    c: Tangent(g12,g13) = 1.5708
    c: Equal(g13,g10)
    c: Coincident(g14,g7)
    c: Diameter(g14) = 3.4
FEATURE [PartDesign::Pocket] Pocket042
  BaseFeature = -> Pocket041
  Direction = (0,0,-1)
  Length = 5
  Length2 = 5
  Midplane = true
  Profile = -> Sketch084
  ReferenceAxis = -> Sketch084 [N_Axis]
  Type = 1
FEATURE [PartDesign::Body] Body001003005003013  label="plexiglass_holder_top"
  Group = -> [Sketch082,Pad021,Sketch083,Mirrored029,Pocket041,Sketch084,Pocket042]
  Origin = -> Origin026
  Placement = pos=(0,0,0) rot=(0,0,1;1.0472rad)
  Tip = -> Pocket042
COMPONENT P9 — recipe-attached ("corner_72x15_material_0.30ansi", modeled in this document).
Construction recipe (the document's own serialized feature program — sketch geometry with constraints, then the solid features built on it; lengths are millimeters unless a unit is written):

FEATURE [Sketcher::SketchObject] Sketch085
  FullyConstrained = true
  MapMode = 5
  Placement = pos=(0,0,0) rot=(0.57735,0.57735,0.57735;2.0944rad)
  Support = -> [YZ_Plane028]
  sketch-geometry (2):
    g0: LineSegment StartX=0 StartY=23 StartZ=0 EndX=0 EndY=0 EndZ=0
    g1: LineSegment StartX=0 StartY=0 StartZ=0 EndX=23 EndY=0 EndZ=0
  constraints (6):
    c: PointOnObject(g0,g-2)
    c: Coincident(g0,g-1)
    c: Coincident(g1,g0)
    c: PointOnObject(g1,g-1)
    c: Equal(g1,g0)
    c: DistanceX(g1,g1) = 23  'length'
FEATURE [PartDesign::FeaturePython] BaseBend002  # WARN: FeaturePython — macro-defined, semantics opaque (R4)
  BendSide = 0
  BendSketch = -> Sketch085
  MidPlane = true
  Reverse = false
  length = 86
  radius = 2
  thickness = 0.5
FEATURE [Sketcher::SketchObject] Sketch086
  AttachmentOffset = pos=(43,23,0) rot=(0,0,1;0rad)
  FullyConstrained = true
  MapMode = 5
  Placement = pos=(43,23,0) rot=(0,0,1;0rad)
  Support = -> [XY_Plane029]
  expr: .AttachmentOffset.Base.x = BaseBend002.length / 2
  expr: .AttachmentOffset.Base.y = Sketch085.Constraints.length
  sketch-geometry (3):
    g0: ArcOfCircle CenterX=-7.5 CenterY=-7.5 CenterZ=0 NormalX=0 NormalY=0 NormalZ=1 AngleXU=0 Radius=7.5 StartAngle=0 EndAngle=1.5708
    g1: LineSegment StartX=0 StartY=-7.5 StartZ=0 EndX=0 EndY=0 EndZ=0
    g2: LineSegment StartX=0 StartY=0 StartZ=0 EndX=-7.50003 EndY=-6.21876e-11 EndZ=0
  constraints (8):
    c: PointOnObject(g0,g-2)
    c: PointOnObject(g0,g-1)
    c: Coincident(g1,g-1)
    c: Coincident(g2,g1)
    c: Coincident(g2,g0)
    c: Tangent(g2,g0)
    c: Tangent(g1,g0) = -1.5708
    c: Diameter(g0) = 15
FEATURE [PartDesign::Pocket] Pocket047
  BaseFeature = -> BaseBend002
  Direction = (0,0,-1)
  Length = 5
  Length2 = 5
  Midplane = true
  Profile = -> Sketch086
  ReferenceAxis = -> Sketch086 [N_Axis]
  Type = 1
FEATURE [PartDesign::Mirrored] Mirrored032
  MirrorPlane = -> YZ_Plane028
FEATURE [PartDesign::PolarPattern] PolarPattern010
  Angle = 90
  Axis = -> X_Axis028
  Occurrences = 2
FEATURE [PartDesign::MultiTransform] MultiTransform011
  BaseFeature = -> Pocket047
  Originals = -> [Pocket047]
  Transformations = -> [Mirrored032,PolarPattern010]
FEATURE [Sketcher::SketchObject] Sketch087
  AttachmentOffset = pos=(0,14.5,0) rot=(0,0,1;0rad)
  FullyConstrained = true
  MapMode = 5
  Placement = pos=(0,14.5,0) rot=(0,0,1;0rad)
  Support = -> [XY_Plane029]
  expr: .AttachmentOffset.Base.y = 14.5mm
  expr: Constraints[3] = <<main>>.rivet_d
  sketch-geometry (2):
    g0: Circle CenterX=36 CenterY=0 CenterZ=0 NormalX=0 NormalY=0 NormalZ=1 AngleXU=0 Radius=1.7
    g1: Circle CenterX=-36 CenterY=0 CenterZ=0 NormalX=0 NormalY=0 NormalZ=1 AngleXU=0 Radius=1.7
  constraints (5):
    c: PointOnObject(g0,g-1)
    c: Symmetric(g1,g0,g-1)
    c: Equal(g0,g1)
    c: Diameter(g0) = 3.4
    c: DistanceX(g1,g0) = 72
FEATURE [PartDesign::Pocket] Pocket048
  BaseFeature = -> MultiTransform011
  Direction = (0,0,-1)
  Length = 5
  Length2 = 5
  Midplane = true
  Profile = -> Sketch087
  ReferenceAxis = -> Sketch087 [N_Axis]
  Type = 1
FEATURE [PartDesign::PolarPattern] PolarPattern011
  Angle = 90
  Axis = -> X_Axis028
  BaseFeature = -> Pocket048
  Occurrences = 2
  Originals = -> [Pocket048]
FEATURE [PartDesign::CoordinateSystem] Local_CS031
  AttacherType = Attacher::AttachEngine3D
  MapMode = 2
  Placement = pos=(0,14.5,0) rot=(0,0,1;0rad)
  Support = -> [Sketch087]
FEATURE [PartDesign::Body] Body001003005003015  label="corner_72x15_material_0.30ansi"
  Group = -> [Sketch085,BaseBend002,Sketch086,Pocket047,MultiTransform011,Mirrored032,PolarPattern010,Sketch087,Pocket048,PolarPattern011,Local_CS031]
  Origin = -> Origin028
  Tip = -> PolarPattern011
COMPONENT P10 — recipe-attached ("corner_5.5_material_0.30ansi", modeled in this document).
Construction recipe (the document's own serialized feature program — sketch geometry with constraints, then the solid features built on it; lengths are millimeters unless a unit is written):

FEATURE [PartDesign::Mirrored] Mirrored039
  MirrorPlane = -> YZ_Plane036
FEATURE [PartDesign::PolarPattern] PolarPattern014
  Angle = 90
  Axis = -> X_Axis036
  Occurrences = 2
FEATURE [Sketcher::SketchObject] Sketch108
  FullyConstrained = true
  MapMode = 5
  Placement = pos=(0,0,0) rot=(0.57735,0.57735,0.57735;2.0944rad)
  Support = -> [YZ_Plane036]
  sketch-geometry (2):
    g0: LineSegment StartX=0 StartY=23 StartZ=0 EndX=0 EndY=0 EndZ=0
    g1: LineSegment StartX=0 StartY=0 StartZ=0 EndX=23 EndY=0 EndZ=0
  constraints (6):
    c: PointOnObject(g0,g-2)
    c: Coincident(g0,g-1)
    c: Coincident(g1,g0)
    c: PointOnObject(g1,g-1)
    c: Equal(g1,g0)
    c: DistanceX(g1,g1) = 23  'length'
FEATURE [PartDesign::FeaturePython] BaseBend007  # WARN: FeaturePython — macro-defined, semantics opaque (R4)
  BendSide = 0
  BendSketch = -> Sketch108
  MidPlane = true
  Reverse = false
  length = 86
  radius = 2
  thickness = 0.5
FEATURE [Sketcher::SketchObject] Sketch109
  AttachmentOffset = pos=(43,23,0) rot=(0,0,1;0rad)
  FullyConstrained = true
  MapMode = 5
  Placement = pos=(43,23,0) rot=(0,0,1;0rad)
  Support = -> [XY_Plane037]
  expr: .AttachmentOffset.Base.x = BaseBend007.length / 2
  expr: .AttachmentOffset.Base.y = Sketch108.Constraints.length
  sketch-geometry (3):
    g0: ArcOfCircle CenterX=-7.5 CenterY=-7.5 CenterZ=0 NormalX=0 NormalY=0 NormalZ=1 AngleXU=0 Radius=7.5 StartAngle=0 EndAngle=1.5708
    g1: LineSegment StartX=0 StartY=-7.5 StartZ=0 EndX=0 EndY=0 EndZ=0
    g2: LineSegment StartX=0 StartY=0 StartZ=0 EndX=-7.50003 EndY=-6.21876e-11 EndZ=0
  constraints (8):
    c: PointOnObject(g0,g-2)
    c: PointOnObject(g0,g-1)
    c: Coincident(g1,g-1)
    c: Coincident(g2,g1)
    c: Coincident(g2,g0)
    c: Tangent(g2,g0)
    c: Tangent(g1,g0) = -1.5708
    c: Diameter(g0) = 15
FEATURE [PartDesign::Pocket] Pocket063
  BaseFeature = -> BaseBend007
  Direction = (0,0,-1)
  Length = 5
  Length2 = 5
  Midplane = true
  Profile = -> Sketch109
  ReferenceAxis = -> Sketch109 [N_Axis]
  Type = 1
FEATURE [PartDesign::MultiTransform] MultiTransform013
  BaseFeature = -> Pocket063
  Originals = -> [Pocket063]
  Transformations = -> [Mirrored039,PolarPattern014]
FEATURE [Sketcher::SketchObject] Sketch110
  AttachmentOffset = pos=(0,14.5,0) rot=(0,0,1;0rad)
  FullyConstrained = true
  MapMode = 5
  Placement = pos=(0,-3.2e-15,14.5) rot=(1,0,0;1.5708rad)
  Support = -> [XZ_Plane036]
  expr: .AttachmentOffset.Base.y = 14.5mm
  expr: Constraints[3] = <<main>>.rivet_d
  sketch-geometry (2):
    g0: Circle CenterX=36 CenterY=0 CenterZ=0 NormalX=0 NormalY=0 NormalZ=1 AngleXU=0 Radius=1.7
    g1: Circle CenterX=-36 CenterY=0 CenterZ=0 NormalX=0 NormalY=0 NormalZ=1 AngleXU=0 Radius=1.7
  constraints (5):
    c: PointOnObject(g0,g-1)
    c: Symmetric(g1,g0,g-1)
    c: Equal(g0,g1)
    c: Diameter(g0) = 3.4
    c: DistanceX(g1,g0) = 72
FEATURE [PartDesign::CoordinateSystem] Local_CS034
  AttacherType = Attacher::AttachEngine3D
  MapMode = 2
  Placement = pos=(0,-3.2e-15,14.5) rot=(1,0,0;1.5708rad)
  Support = -> [Sketch110]
FEATURE [PartDesign::Pocket] Pocket064
  BaseFeature = -> MultiTransform013
  Direction = (0,1,2e-16)
  Length = 5
  Length2 = 5
  Midplane = true
  Profile = -> Sketch110
  ReferenceAxis = -> Sketch110 [N_Axis]
  Type = 1
FEATURE [Sketcher::SketchObject] Sketch111
  AttachmentOffset = pos=(0,14.5,0) rot=(0,0,1;0rad)
  FullyConstrained = true
  MapMode = 5
  Placement = pos=(0,14.5,0) rot=(0,0,1;0rad)
  Support = -> [XY_Plane037]
  expr: .AttachmentOffset.Base.y = Sketch110.AttachmentOffset.Base.y
  expr: Constraints[3] = 5.5
  expr: Constraints[4] = Sketch110.Constraints[4]
  sketch-geometry (2):
    g0: Circle CenterX=36 CenterY=0 CenterZ=0 NormalX=0 NormalY=0 NormalZ=1 AngleXU=0 Radius=2.75
    g1: Circle CenterX=-36 CenterY=0 CenterZ=0 NormalX=0 NormalY=0 NormalZ=1 AngleXU=0 Radius=2.75
  constraints (5):
    c: PointOnObject(g0,g-1)
    c: Symmetric(g1,g0,g-1)
    c: Equal(g0,g1)
    c: Diameter(g0) = 5.5
    c: DistanceX(g1,g0) = 72
FEATURE [PartDesign::Pocket] Pocket065
  BaseFeature = -> Pocket064
  Direction = (0,0,-1)
  Length = 5
  Length2 = 5
  Midplane = true
  Profile = -> Sketch111
  ReferenceAxis = -> Sketch111 [N_Axis]
  Type = 1
FEATURE [PartDesign::Body] Body001003005003015002  label="corner_5.5_material_0.30ansi"
  Group = -> [Sketch108,BaseBend007,Sketch109,Pocket063,MultiTransform013,Mirrored039,PolarPattern014,Sketch110,Pocket064,Local_CS034,Sketch111,Pocket065]
  Origin = -> Origin036
  Tip = -> Pocket065
COMPONENT P11 — recipe-attached ("Body001003005003015005", modeled in this document).
Construction recipe (the document's own serialized feature program — sketch geometry with constraints, then the solid features built on it; lengths are millimeters unless a unit is written):

FEATURE [Sketcher::SketchObject] Sketch131
  FullyConstrained = true
  MapMode = 5
  Support = -> [XY_Plane042]
  sketch-geometry (5):
    g0: LineSegment StartX=-20 StartY=20 StartZ=0 EndX=-20 EndY=0 EndZ=0
    g1: LineSegment StartX=-20 StartY=0 StartZ=0 EndX=20 EndY=0 EndZ=0
    g2: LineSegment StartX=20 StartY=0 StartZ=0 EndX=20 EndY=20 EndZ=0
    g3: LineSegment StartX=20 StartY=20 StartZ=0 EndX=-20 EndY=20 EndZ=0
    g4: GeomPoint X=0 Y=10 Z=0
  constraints (13):
    c: Coincident(g0,g1)
    c: Coincident(g1,g2)
    c: Coincident(g2,g3)
    c: Coincident(g3,g0)
    c: Horizontal(g1)
    c: Horizontal(g3)
    c: Vertical(g0)
    c: Vertical(g2)
    c: Symmetric(g1,g0,g4)
    c: PointOnObject(g4,g-2)
    c: PointOnObject(g1,g-1)
    c: DistanceX(g1,g1) = 40
    c: DistanceY(g2) = 20
FEATURE [PartDesign::Pad] Pad029
  Direction = (0,0,1)
  Length = 1.5
  Length2 = 10
  Profile = -> Sketch131
  ReferenceAxis = -> Sketch131 [N_Axis]
  Type = 0
FEATURE [PartDesign::Body] Body001003005003015005
  Group = -> [Sketch131,Pad029]
  Origin = -> Origin041
  Tip = -> Pad029
COMPONENT P12 — recipe-attached ("Unfold_main", modeled in this document).
Construction recipe (the document's own serialized feature program — sketch geometry with constraints, then the solid features built on it; lengths are millimeters unless a unit is written):

FEATURE [PartDesign::FeatureBase] BaseFeature001
  BaseFeature = -> Unfold011
  Placement = pos=(0,0,208.372) rot=(0.57735,0.57735,-0.57735;4.18879rad)
  expr: Placement = <<Unfold>>.Placement
FEATURE [PartDesign::Pad] Pad031
  BaseFeature = -> BaseFeature001
  Direction = (-3e-16,5e-16,1)
  Length = 2.7
  Length2 = 10
  Placement = pos=(0,0,208.372) rot=(0.57735,0.57735,-0.57735;4.18879rad)
  Profile = -> BaseFeature001 [Face543]
  Type = 0
FEATURE [PartDesign::Body] Body001003005003015006  label="Unfold_main"
  BaseFeature = -> Unfold011
  Group = -> [BaseFeature001,Pad031]
  Origin = -> Origin042
  Tip = -> Pad031
COMPONENT P13 — recipe-attached ("Unfold_top", modeled in this document).
Construction recipe (the document's own serialized feature program — sketch geometry with constraints, then the solid features built on it; lengths are millimeters unless a unit is written):

FEATURE [PartDesign::FeatureBase] BaseFeature002
  BaseFeature = -> Unfold014
  Placement = pos=(0,0,0) rot=(0.707107,0.707107,0;3.14159rad)
  expr: Placement = Unfold014.Placement
FEATURE [PartDesign::Pad] Pad032
  BaseFeature = -> BaseFeature002
  Direction = (0,2e-16,1)
  Length = 2.7
  Length2 = 10
  Placement = pos=(0,0,0) rot=(0.707107,0.707107,0;3.14159rad)
  Profile = -> BaseFeature002 [Face2]
  Type = 0
FEATURE [PartDesign::Body] Body001003005003015007  label="Unfold_top"
  BaseFeature = -> Unfold014
  Group = -> [BaseFeature002,Pad032]
  Origin = -> Origin043
  Tip = -> Pad032
COMPONENT P14 — recipe-attached ("top_material_0.50ansi", modeled in this document).
Construction recipe (the document's own serialized feature program — sketch geometry with constraints, then the solid features built on it; lengths are millimeters unless a unit is written):

FEATURE [PartDesign::CoordinateSystem] LCS_0
  AttacherType = Attacher::AttachEngine3D
  MapMode = 2
  Support = -> [X_Axis029]
FEATURE [Sketcher::SketchObject] Sketch089
  FullyConstrained = true
  MapMode = 5
  Placement = pos=(0,0,0) rot=(1,0,0;1.5708rad)
  Support = -> [XZ_Plane029]
  sketch-geometry (5):
    g0: LineSegment StartX=-41.5 StartY=-36.5 StartZ=0 EndX=-41.5 EndY=0 EndZ=0
    g1: LineSegment StartX=-41.5 StartY=0 StartZ=0 EndX=41.5 EndY=0 EndZ=0
    g2: LineSegment StartX=41.5 StartY=0 StartZ=0 EndX=41.5 EndY=-36.5 EndZ=0
    g3: LineSegment StartX=41.5 StartY=-36.5 StartZ=0 EndX=-41.5 EndY=-36.5 EndZ=0
    g4: GeomPoint X=0 Y=-18.25 Z=0
  constraints (13):
    c: Coincident(g0,g1)
    c: Coincident(g1,g2)
    c: Coincident(g2,g3)
    c: Coincident(g3,g0)
    c: Horizontal(g1)
    c: Horizontal(g3)
    c: Vertical(g0)
    c: Vertical(g2)
    c: Symmetric(g1,g0,g4)
    c: PointOnObject(g4,g-2)
    c: PointOnObject(g1,g-1)
    c: DistanceX(g1,g1) = 83  'width'
    c: DistanceY(g2,g2) = 36.5
FEATURE [PartDesign::FeaturePython] BaseBend003  # WARN: FeaturePython — macro-defined, semantics opaque (R4)
  BendSide = 0
  BendSketch = -> Sketch089
  MidPlane = true
  Reverse = false
  length = 108.4
  radius = 0.01
  thickness = 0.3
  expr: radius = <<main>>.bend_r
FEATURE [Sketcher::SketchObject] Sketch090
  FullyConstrained = true
  MapMode = 5
  Support = -> [XY_Plane030]
  expr: Constraints[6] = <<main>>.end_face_width / 2
  sketch-geometry (6):
    g0: LineSegment StartX=0 StartY=-100 StartZ=0 EndX=14.5 EndY=-100 EndZ=0
    g1: LineSegment StartX=16 StartY=-98.5 StartZ=0 EndX=16 EndY=100 EndZ=0
    g2: LineSegment StartX=16 StartY=100 StartZ=0 EndX=0 EndY=109.238 EndZ=0
    g3: LineSegment StartX=0 StartY=109.238 StartZ=0 EndX=0 EndY=-100 EndZ=0
    g4: ArcOfCircle CenterX=14.5 CenterY=-98.5 CenterZ=0 NormalX=0 NormalY=0 NormalZ=1 AngleXU=0 Radius=1.5 StartAngle=4.71239 EndAngle=6.28319
    g5: GeomPoint X=16 Y=-100 Z=0
  constraints (15):
    c: Coincident(g1,g2)
    c: Coincident(g2,g3)
    c: Coincident(g3,g0)
    c: Horizontal(g0)
    c: Vertical(g3)
    c: PointOnObject(g0,g-2)
    c: DistanceX(g5) = 16
    c: Angle(g-2,g2) = 1.0472
    c: Symmetric(g1,g5,g-1)
    c: DistanceY(g5,g1) = 200
    c: PointOnObject(g5,g0)
    c: PointOnObject(g5,g1)
    c: Tangent(g0,g4) = -1.5708
    c: Tangent(g1,g4) = -1.5708
    c: Diameter(g4) = 3
FEATURE [PartDesign::Pad] Pad023
  BaseFeature = -> BaseBend003
  Direction = (0,0,1)
  Length = 0.3
  Length2 = 10
  Profile = -> Sketch090
  ReferenceAxis = -> Sketch090 [N_Axis]
  Reversed = true
  Type = 0
FEATURE [PartDesign::Mirrored] Mirrored034
  BaseFeature = -> Pad023
  MirrorPlane = -> Sketch090 [V_Axis]
  Originals = -> [Pad023]
  Refine = true
FEATURE [Sketcher::SketchObject] Sketch091
  FullyConstrained = true
  MapMode = 5
  Placement = pos=(0,0,0) rot=(0.57735,0.57735,0.57735;2.0944rad)
  Support = -> [YZ_Plane029]
  sketch-geometry (8):
    g0: LineSegment StartX=0 StartY=-36.5 StartZ=0 EndX=0 EndY=-18.63 EndZ=0
    g1: LineSegment StartX=0 StartY=-18.63 StartZ=0 EndX=17.4865 EndY=-18.63 EndZ=0
    g2: LineSegment StartX=54.2 StartY=-36.5 StartZ=0 EndX=54.2 EndY=-18.63 EndZ=0
    g3: ArcOfCircle CenterX=36.33 CenterY=-18.63 CenterZ=0 NormalX=0 NormalY=0 NormalZ=1 AngleXU=0 Radius=17.87 StartAngle=4.71239 EndAngle=6.28319
    g4: LineSegment StartX=54.2 StartY=-36.5 StartZ=0 EndX=36.33 EndY=-36.5 EndZ=0
    g5: ArcOfCircle CenterX=36.33 CenterY=-18.63 CenterZ=0 NormalX=0 NormalY=0 NormalZ=1 AngleXU=0 Radius=17.87 StartAngle=3.19461 EndAngle=4.71239
    g6: ArcOfCircle CenterX=17.4865 CenterY=-19.63 CenterZ=0 NormalX=0 NormalY=0 NormalZ=1 AngleXU=0 Radius=1 StartAngle=0.053019 EndAngle=1.5708
    g7: LineSegment StartX=0 StartY=-36.5 StartZ=0 EndX=36.33 EndY=-36.5 EndZ=0
  constraints (22):
    c: PointOnObject(g0,g-2)
    c: PointOnObject(g0,g-2)
    c: Coincident(g0,g1)
    c: Horizontal(g1)
    c: Vertical(g2)
    c: Coincident(g4,g2)
    c: Horizontal(g4)
    c: Tangent(g3,g2) = -1.5708
    c: Coincident(g5,g3)
    c: Coincident(g5,g3)
    c: Tangent(g1,g6) = 1.5708
    c: Tangent(g6,g5) = 1.5708
    c: Coincident(g7,g0)
    c: Coincident(g7,g3)
    c: Horizontal(g7)
    c: Coincident(g3,g4)
    c: Tangent(g5,g7)
    c: DistanceY(g0) = -36.5
    c: DistanceX(g2) = 54.2
    c: Diameter(g6) = 2
    c: Diameter(g5) = 35.74
    c: Horizontal(g0,g2)
FEATURE [PartDesign::Pocket] Pocket050
  BaseFeature = -> Mirrored034
  Direction = (-1,2e-16,-3e-16)
  Length = 5
  Length2 = 5
  Midplane = true
  Profile = -> Sketch091
  ReferenceAxis = -> Sketch091 [N_Axis]
  Refine = true
  Type = 1
FEATURE [PartDesign::Mirrored] Mirrored035
  BaseFeature = -> Pocket050
  MirrorPlane = -> Sketch091 [V_Axis]
  Originals = -> [Pocket050]
FEATURE [Sketcher::SketchObject] Sketch092
  FullyConstrained = true
  MapMode = 5
  Placement = pos=(0,0,0) rot=(0.57735,0.57735,0.57735;2.0944rad)
  Support = -> [YZ_Plane029]
  sketch-geometry (1):
    g0: Circle CenterX=0 CenterY=-9.63 CenterZ=0 NormalX=0 NormalY=0 NormalZ=1 AngleXU=0 Radius=1.65
  constraints (3):
    c: PointOnObject(g0,g-2)
    c: Diameter(g0) = 3.3
    c: DistanceY(g0) = -9.63
FEATURE [PartDesign::Pocket] Pocket051
  BaseFeature = -> Mirrored035
  Direction = (-1,2e-16,-3e-16)
  Length = 5
  Length2 = 5
  Midplane = true
  Profile = -> Sketch092
  ReferenceAxis = -> Sketch092 [N_Axis]
  Type = 1
FEATURE [PartDesign::Body] Body_2  label="top_material_0.50ansi"
  Group = -> [LCS_0,Sketch089,BaseBend003,Sketch090,Pad023,Mirrored034,Sketch091,Pocket050,Mirrored035,Sketch092,Pocket051]
  Origin = -> Origin029
  Placement = pos=(0,0,3) rot=(0,0,1;0rad)
  Tip = -> Pocket051
COMPONENT P15 — recipe-attached ("top_small_material_0.50ansi", modeled in this document).
Construction recipe (the document's own serialized feature program — sketch geometry with constraints, then the solid features built on it; lengths are millimeters unless a unit is written):

FEATURE [PartDesign::CoordinateSystem] LCS_0001
  AttacherType = Attacher::AttachEngine3D
  MapMode = 2
  Support = -> [X_Axis030]
FEATURE [Sketcher::SketchObject] Sketch093  label="Stainless_top_Sketch"
  FullyConstrained = true
  MapMode = 5
  Placement = pos=(0,0,0) rot=(1,0,0;1.5708rad)
  Support = -> [XZ_Plane030]
  sketch-geometry (5):
    g0: LineSegment StartX=-38 StartY=-33.5 StartZ=0 EndX=-38 EndY=0 EndZ=0
    g1: LineSegment StartX=-38 StartY=0 StartZ=0 EndX=38 EndY=0 EndZ=0
    g2: LineSegment StartX=38 StartY=0 StartZ=0 EndX=38 EndY=-33.5 EndZ=0
    g3: LineSegment StartX=38 StartY=-33.5 StartZ=0 EndX=-38 EndY=-33.5 EndZ=0
    g4: GeomPoint X=0 Y=-16.75 Z=0
  constraints (13):
    c: Coincident(g0,g1)
    c: Coincident(g1,g2)
    c: Coincident(g2,g3)
    c: Coincident(g3,g0)
    c: Horizontal(g1)
    c: Horizontal(g3)
    c: Vertical(g0)
    c: Vertical(g2)
    c: Symmetric(g1,g0,g4)
    c: PointOnObject(g4,g-2)
    c: PointOnObject(g1,g-1)
    c: DistanceX(g1,g1) = 76  'width'
    c: DistanceY(g2,g1) = 33.5  'height'
FEATURE [PartDesign::FeaturePython] BaseBend004  # WARN: FeaturePython — macro-defined, semantics opaque (R4)
  BendSide = 0
  BendSketch = -> Sketch093
  MidPlane = true
  Reverse = false
  length = 108.4
  radius = 2
  thickness = 0.5
  expr: length = BaseBend003.length
FEATURE [PartDesign::SubShapeBinder] Binder024
  BindCopyOnChange = 0
  BindMode = 0
  ClaimChildren = false
  Context = -> Body_3 [Binder024.]
  Fuse = false
  MakeFace = true
  OffsetFill = true
  OffsetIntersection = false
  OffsetJoinType = 0
  OffsetOpenResult = true
  PartialLoad = false
  Relative = true
  Support = -> [Body_2[Pocket050.Sketch091.]]
  _Version = 2
FEATURE [PartDesign::Pocket] Pocket052
  BaseFeature = -> BaseBend004
  Direction = (-1,2e-16,-2e-16)
  Length = 5
  Length2 = 5
  Midplane = true
  Profile = -> Binder024 [Face1]
  Type = 1
FEATURE [PartDesign::Mirrored] Mirrored036
  BaseFeature = -> Pocket052
  MirrorPlane = -> XZ_Plane030
  Originals = -> [Pocket052]
FEATURE [PartDesign::SubShapeBinder] Binder025
  BindCopyOnChange = 0
  BindMode = 0
  ClaimChildren = false
  Context = -> Body_3 [Binder025.]
  Fuse = false
  MakeFace = true
  OffsetFill = false
  OffsetIntersection = false
  OffsetJoinType = 0
  OffsetOpenResult = false
  PartialLoad = false
  Relative = true
  Support = -> [Body_2[Pocket051.Sketch092.]]
  _Version = 2
FEATURE [PartDesign::Pocket] Pocket053
  BaseFeature = -> Mirrored036
  Direction = (-1,2e-16,-2e-16)
  Length = 5
  Length2 = 5
  Midplane = true
  Profile = -> Binder025
  Type = 1
FEATURE [PartDesign::SubShapeBinder] Binder031
  BindCopyOnChange = 0
  BindMode = 0
  ClaimChildren = false
  Context = -> Body_3 [Binder031.]
  Fuse = false
  MakeFace = true
  OffsetFill = false
  OffsetIntersection = false
  OffsetJoinType = 0
  OffsetOpenResult = false
  PartialLoad = false
  Relative = true
  _Version = 2
FEATURE [PartDesign::Pocket] Pocket060
  BaseFeature = -> Pocket053
  Direction = (0,0,-1)
  Length = 5
  Length2 = 5
  Midplane = true
  Profile = -> Binder031
  Type = 1
FEATURE [PartDesign::Body] Body_3  label="top_small_material_0.50ansi"
  Group = -> [LCS_0001,Sketch093,BaseBend004,Binder024,Pocket052,Mirrored036,Binder025,Pocket053,Pocket060,Binder031]
  Origin = -> Origin030
  Tip = -> Pocket060
COMPONENT P16 — recipe-attached ("vodostok_s_material_0.30ansi", modeled in this document).
Construction recipe (the document's own serialized feature program — sketch geometry with constraints, then the solid features built on it; lengths are millimeters unless a unit is written):

FEATURE [PartDesign::CoordinateSystem] LCS_0002
  AttacherType = Attacher::AttachEngine3D
  MapMode = 2
  Support = -> [X_Axis032]
FEATURE [Sketcher::SketchObject] Sketch094
  FullyConstrained = true
  MapMode = 5
  Support = -> [XY_Plane033]
  expr: Constraints[5] = <<main>>.rivet_d
  expr: Constraints[6] = <<module>>.module_width + 24mm
  sketch-geometry (3):
    g0: Circle CenterX=-86 CenterY=2e-16 CenterZ=0 NormalX=0 NormalY=0 NormalZ=1 AngleXU=0 Radius=1.7
    g1: Circle CenterX=86 CenterY=0 CenterZ=0 NormalX=0 NormalY=0 NormalZ=1 AngleXU=0 Radius=1.7
    g2: Circle CenterX=86 CenterY=-45 CenterZ=0 NormalX=0 NormalY=0 NormalZ=1 AngleXU=0 Radius=1.7
  constraints (8):
    c: PointOnObject(g1,g-1)
    c: Vertical(g2,g1)
    c: Symmetric(g0,g1,g-2)
    c: Equal(g0,g1)
    c: Equal(g1,g2)
    c: Diameter(g1) = 3.4
    c: DistanceX(g0,g1) = 172
    c: DistanceY(g2,g1) = 45
FEATURE [Sketcher::SketchObject] Sketch095
  FullyConstrained = true
  MapMode = 5
  Support = -> [XY_Plane033]
  expr: Constraints[31] = 10
  expr: Constraints[43] = <<module>>.module_width + 24mm
  expr: Constraints[44] = <<module>>.module_width
  sketch-geometry (31):
    g0: LineSegment StartX=96 StartY=-87.0059 StartZ=0 EndX=96 EndY=5 EndZ=0
    g1: LineSegment StartX=91 StartY=10 StartZ=0 EndX=-91 EndY=10 EndZ=0
    g2: LineSegment StartX=-96 StartY=5 StartZ=0 EndX=-96 EndY=-5 EndZ=0
    g3: LineSegment StartX=-91 StartY=-10 StartZ=0 EndX=-77 EndY=-10 EndZ=0
    g4: LineSegment StartX=-72 StartY=-15 StartZ=0 EndX=-72 EndY=-59.848 EndZ=0
    g5: LineSegment StartX=-48.163 StartY=-99.1271 StartZ=0 EndX=88.7532 EndY=-94.5016 EndZ=0
    g6: ArcOfCircle CenterX=91 CenterY=5 CenterZ=0 NormalX=0 NormalY=0 NormalZ=1 AngleXU=0 Radius=5 StartAngle=0 EndAngle=1.5708
    g7: GeomPoint X=96 Y=10 Z=0
    g8: ArcOfCircle CenterX=-91 CenterY=-5 CenterZ=0 NormalX=0 NormalY=0 NormalZ=1 AngleXU=0 Radius=5 StartAngle=3.14159 EndAngle=4.71239
    g9: GeomPoint X=-96 Y=-10 Z=0
    g10: ArcOfCircle CenterX=-91 CenterY=5 CenterZ=0 NormalX=0 NormalY=0 NormalZ=1 AngleXU=0 Radius=5 StartAngle=1.5708 EndAngle=3.14159
    g11: GeomPoint X=-96 Y=10 Z=0
    g12: ArcOfCircle CenterX=-77 CenterY=-15 CenterZ=0 NormalX=0 NormalY=0 NormalZ=1 AngleXU=0 Radius=5 StartAngle=0 EndAngle=1.5708
    g13: GeomPoint X=-72 Y=-10 Z=0
    g14: GeomPoint X=-72 Y=-99.9324 Z=0
    g15: ArcOfCircle CenterX=88.5 CenterY=-87.0059 CenterZ=0 NormalX=0 NormalY=0 NormalZ=1 AngleXU=0 Radius=7.5 StartAngle=4.74616 EndAngle=6.28319
    g16: GeomPoint X=96 Y=-94.2568 Z=0
    g17: LineSegment StartX=-72 StartY=-59.9324 StartZ=0 EndX=96 EndY=-54.2568 EndZ=0
    g18: LineSegment StartX=-91 StartY=5 StartZ=0 EndX=-91 EndY=0 EndZ=0
    g19: LineSegment StartX=-91 StartY=0 StartZ=0 EndX=-91 EndY=-5 EndZ=0
    g20: GeomPoint X=86 Y=0 Z=0
    g21: GeomPoint X=-86 Y=0 Z=0
    g22: GeomPoint X=74 Y=0 Z=0
    g23: GeomPoint X=-74 Y=0 Z=0
    g24: LineSegment StartX=-91 StartY=-5 StartZ=0 EndX=-86 EndY=0 EndZ=0
    g25: GeomPoint X=-74 Y=-60 Z=0
    g26: GeomPoint X=74 Y=-55 Z=0
    g27: LineSegment StartX=-71.9971 StartY=-60.0168 StartZ=0 EndX=-71.4099 EndY=-77.3997 EndZ=0
    g28: ArcOfCircle CenterX=-48.9227 CenterY=-76.64 CenterZ=0 NormalX=0 NormalY=0 NormalZ=1 AngleXU=0 Radius=22.5 StartAngle=3.17536 EndAngle=4.74616
    g29: ArcOfCircle CenterX=-67 CenterY=-59.848 CenterZ=0 NormalX=0 NormalY=0 NormalZ=1 AngleXU=0 Radius=5 StartAngle=3.14159 EndAngle=3.17536
    g30: GeomPoint X=-72 Y=-59.9324 Z=0
  constraints (70):
    c: Vertical(g0)
    c: Horizontal(g1)
    c: Vertical(g2)
    c: Horizontal(g3)
    c: Vertical(g4)
    c: PointOnObject(g7,g1)
    c: PointOnObject(g7,g0)
    c: Tangent(g1,g6) = -1.5708
    c: Tangent(g0,g6) = -1.5708
    c: PointOnObject(g9,g3)
    c: PointOnObject(g9,g2)
    c: Tangent(g3,g8) = -1.5708
    c: Tangent(g2,g8) = -1.5708
    c: PointOnObject(g11,g2)
    c: PointOnObject(g11,g1)
    c: Tangent(g2,g10) = -1.5708
    c: Tangent(g1,g10) = -1.5708
    c: PointOnObject(g13,g3)
    c: PointOnObject(g13,g4)
    c: Tangent(g3,g12) = 1.5708
    c: Tangent(g4,g12) = 1.5708
    c: PointOnObject(g14,g4)
    c: PointOnObject(g14,g5)
    c: PointOnObject(g16,g5)
    c: PointOnObject(g16,g0)
    c: Tangent(g5,g15) = -1.5708
    c: Tangent(g0,g15) = -1.5708
    c: Parallel(g17,g5)
    c: Equal(g12,g8)
    c: Equal(g8,g10)
    c: Equal(g10,g6)
    c: Diameter(g10) = 10
    c: Diameter(g15) = 15
    c: Coincident(g18,g10)
    c: PointOnObject(g18,g-1)
    c: Vertical(g18)
    c: Coincident(g18,g19)
    c: Coincident(g19,g8)
    c: Equal(g19,g18)
    c: PointOnObject(g20,g-1)
    c: PointOnObject(g22,g-1)
    c: Symmetric(g21,g20,g-2)
    c: Symmetric(g23,g22,g-2)
    c: DistanceX(g21,g20) = 172
    c: DistanceX(g23,g22) = 148
    c: DistanceY(g9,g11) = 20
    c: Coincident(g24,g8)
    c: Coincident(g24,g21)
    c: Angle(g24,g-1) = 2.35619
    c: DistanceY(g16,g17) = 40
    c: DistanceX(g22,g0) = 22
    c: Vertical(g22,g26)
    c: Vertical(g25,g23)
    c: DistanceY(g25,g26) = 5
    c: PointOnObject(g26,g17)
    c: PointOnObject(g25,g17)
    c: DistanceY(g26,g22) = 55
    c: Coincident(g30,g17)
    c: Perpendicular(g27,g17)
    c: Tangent(g28,g5) = -1.5708
    c: Tangent(g28,g27) = -1.5708
    c: PointOnObject(g17,g0)
    c: Diameter(g28) = 45
    c: DistanceX(g23,g13) = 2
    c: PointOnObject(g30,g27)
    c: PointOnObject(g30,g4)
    c: Tangent(g27,g29) = -1.5708
    c: Tangent(g4,g29) = -1.5708
    c: Diameter(g29) = 10
    c: Angle(g-1,g17) = 0.0337709
FEATURE [PartDesign::Pad] Pad025
  Direction = (0,0,1)
  Length = 0.5
  Length2 = 10
  Profile = -> Sketch095
  ReferenceAxis = -> Sketch095 [N_Axis]
  Type = 0
FEATURE [Sketcher::SketchObject] Sketch096
  AttachmentOffset = pos=(0,0,0.5) rot=(0,0,1;0rad)
  FullyConstrained = false
  MapMode = 5
  Placement = pos=(0,0,0.5) rot=(0,0,1;0rad)
  Support = -> [XY_Plane033]
  expr: .AttachmentOffset.Base.z = Pad025.Length
  expr: Constraints[4] = <<module>>.module_width
  sketch-geometry (5):
    g0: GeomPoint X=-74 Y=0 Z=0
    g1: GeomPoint X=74 Y=0 Z=0
    g2: GeomPoint X=74 Y=-58 Z=0
    g3: GeomPoint X=-74 Y=-63 Z=0
    g4: LineSegment StartX=-105.813 StartY=-64.0748 StartZ=0 EndX=129.863 EndY=-56.1127 EndZ=0
  constraints (9):
    c: PointOnObject(g1,g-1)
    c: DistanceY(g3,g2) = 5
    c: DistanceY(g2,g1) = 58
    c: Symmetric(g0,g1,g-1)
    c: DistanceX(g0,g1) = 148
    c: Vertical(g2,g1)
    c: Vertical(g3,g0)
    c: PointOnObject(g2,g4)
    c: PointOnObject(g3,g4)
FEATURE [Sketcher::SketchObject] Sketch097
  FullyConstrained = false
  MapMode = 5
  Support = -> [XY_Plane033]
  sketch-geometry (1):
    g0: Circle CenterX=-66 CenterY=-66.2266 CenterZ=0 NormalX=0 NormalY=0 NormalZ=1 AngleXU=0 Radius=2.5
  constraints (2):
    c: Diameter(g0) = 5
    c: DistanceX(g0) = -66
FEATURE [PartDesign::Pocket] Pocket054
  BaseFeature = -> Pad025
  Direction = (0,0,-1)
  Length = 5
  Length2 = 5
  Midplane = true
  Profile = -> Sketch097
  ReferenceAxis = -> Sketch097 [N_Axis]
  Type = 1
FEATURE [PartDesign::Pocket] Pocket055
  BaseFeature = -> Pocket054
  Direction = (0,0,-1)
  Length = 5
  Length2 = 5
  Midplane = true
  Profile = -> Sketch094
  ReferenceAxis = -> Sketch094 [N_Axis]
  Type = 1
FEATURE [PartDesign::FeaturePython] Fold009  # WARN: FeaturePython — macro-defined, semantics opaque (R4)
  BaseFeature = -> Pocket055
  BendLine = -> Sketch096
  Position = 0
  angle = 105
  baseObject = -> Pocket055 [Face5]
  invert = false
  invertbend = false
  kfactor = 0.5
  radius = 2
  unfold = false
FEATURE [PartDesign::Body] Body_4  label="vodostok_s_material_0.30ansi"
  Group = -> [LCS_0002,Sketch094,Sketch095,Pad025,Sketch096,Sketch097,Pocket054,Pocket055,Fold009]
  Origin = -> Origin032
  Tip = -> Fold009
